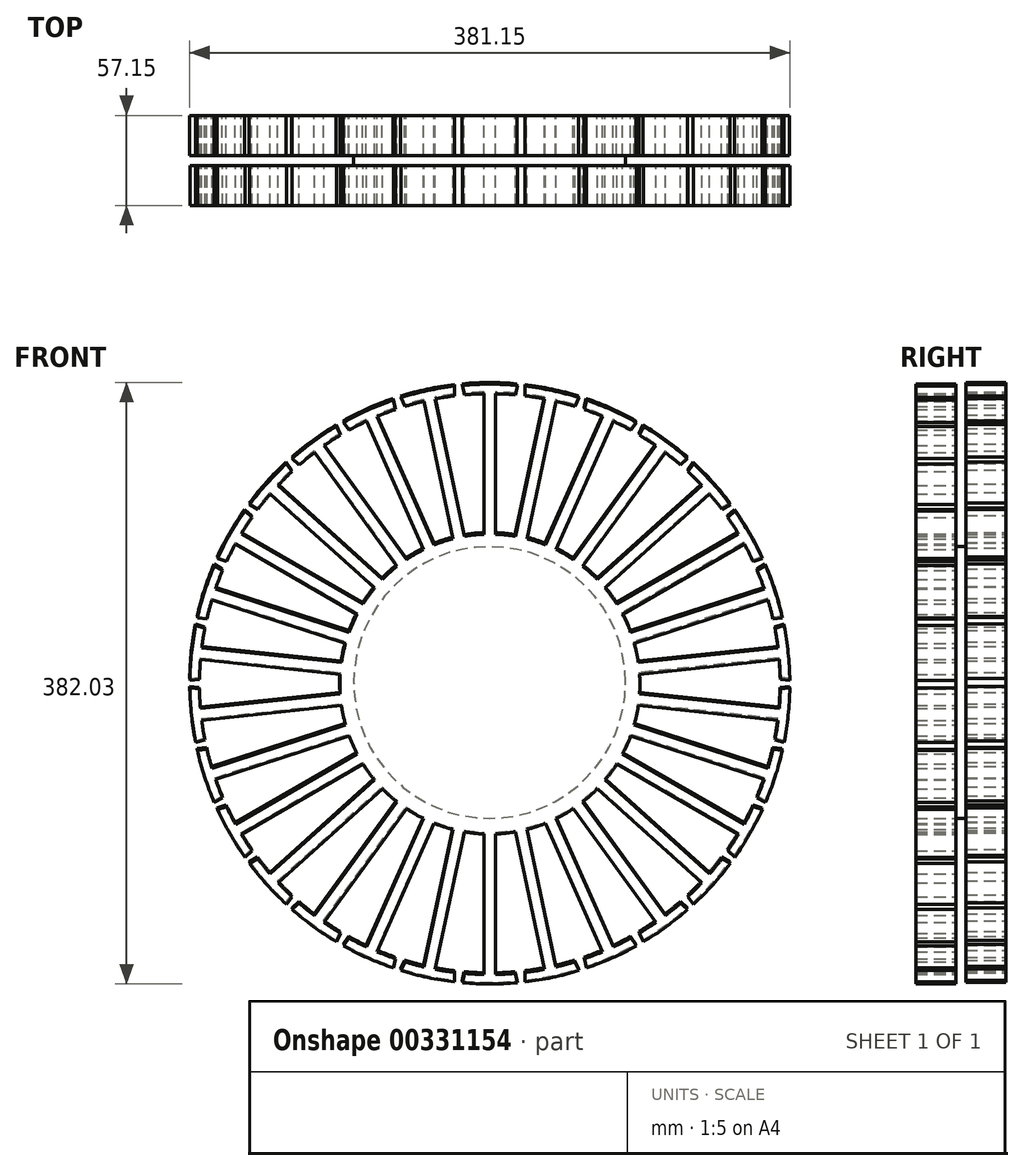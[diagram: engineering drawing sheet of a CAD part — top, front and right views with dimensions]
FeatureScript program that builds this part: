
annotation { "Feature Type Name" : "Feature", "Feature Type Description" : "" }
export const myFeature = defineFeature(function(context is Context, id is Id, definition is map)
    precondition{}
    {
        {
            var Q0;
            Q0=qCreatedBy(makeId("Front.planeOp"),FACE);
            var sketch = newSketch(context, id + "F0", { "sketchPlane" : qUnion([Q0])});
            skArc(sketch, "E0", {"start": v(17.45, 189.7) * mm, "mid": v(0, 190.5) * mm, "end": v(-17.45, 189.7) * mm});
            skArc(sketch, "E1", {"start": v(-3.7, 95.18) * mm, "mid": v(0, -95.25) * mm, "end": v(3.7, 95.18) * mm});
            skArc(sketch, "E2", {"start": v(-3.7, 184.44) * mm, "mid": v(-9.96, 184.2) * mm, "end": v(-16.2, 183.77) * mm});
            skLineSegment(sketch, "E3.left", {"start": v(3.7, 184.44) * mm, "end": v(3.7, 95.18) * mm});
            skLineSegment(sketch, "E3.right", {"start": v(-3.7, 184.44) * mm, "end": v(-3.7, 95.18) * mm});
            skPoint(sketch, "E3.middle", {"position": v(0, 139.8) * mm});
            skLineSegment(sketch, "E4", {"start": v(-17.45, 189.7) * mm, "end": v(-16.2, 183.77) * mm});
            skLineSegment(sketch, "E5.MirrorCS", {"start": v(17.45, 189.7) * mm, "end": v(16.2, 183.77) * mm});
            skArc(sketch, "E6.trimOffspring", {"start": v(16.2, 183.77) * mm, "mid": v(9.96, 184.2) * mm, "end": v(3.7, 184.44) * mm});
            skArc(sketch, "E7.1.0", {"start": v(-22.38, 189.18) * mm, "mid": v(-39.6, 186.34) * mm, "end": v(-56.5, 181.93) * mm});
            skLineSegment(sketch, "E7.1.1", {"start": v(-56.5, 181.93) * mm, "end": v(-54.05, 176.38) * mm});
            skArc(sketch, "E7.1.2", {"start": v(-41.97, 179.64) * mm, "mid": v(-48.04, 178.11) * mm, "end": v(-54.05, 176.38) * mm});
            skArc(sketch, "E7.1.3", {"start": v(-22.36, 183.12) * mm, "mid": v(-28.56, 182.25) * mm, "end": v(-34.73, 181.18) * mm});
            skLineSegment(sketch, "E7.1.4", {"start": v(-22.38, 189.18) * mm, "end": v(-22.36, 183.12) * mm});
            skLineSegment(sketch, "E7.1.5", {"start": v(-34.73, 181.18) * mm, "end": v(-16.17, 93.87) * mm});
            skLineSegment(sketch, "E7.1.6", {"start": v(-41.97, 179.64) * mm, "end": v(-23.41, 92.33) * mm});
            skArc(sketch, "E8.3.2.0", {"start": v(-61.22, 180.4) * mm, "mid": v(-77.48, 174.03) * mm, "end": v(-93.1, 166.2) * mm});
            skLineSegment(sketch, "E8.4.2.0", {"start": v(-93.1, 166.2) * mm, "end": v(-89.54, 161.29) * mm});
            skArc(sketch, "E8.7.2.0", {"start": v(-78.4, 166.99) * mm, "mid": v(-84.02, 164.23) * mm, "end": v(-89.54, 161.29) * mm});
            skArc(sketch, "E8.11.2.0", {"start": v(-59.95, 174.47) * mm, "mid": v(-65.83, 172.33) * mm, "end": v(-71.64, 170) * mm});
            skLineSegment(sketch, "E8.15.2.0", {"start": v(-61.22, 180.4) * mm, "end": v(-59.95, 174.47) * mm});
            skLineSegment(sketch, "E8.18.2.0", {"start": v(-71.64, 170) * mm, "end": v(-35.33, 88.46) * mm});
            skLineSegment(sketch, "E8.21.2.0", {"start": v(-78.4, 166.99) * mm, "end": v(-42.1, 85.44) * mm});
            skArc(sketch, "E8.3.3.0", {"start": v(-97.39, 163.72) * mm, "mid": v(-111.97, 154.12) * mm, "end": v(-125.62, 143.22) * mm});
            skLineSegment(sketch, "E8.4.3.0", {"start": v(-125.62, 143.22) * mm, "end": v(-121.12, 139.15) * mm});
            skArc(sketch, "E8.7.3.0", {"start": v(-111.4, 147.04) * mm, "mid": v(-116.33, 143.18) * mm, "end": v(-121.12, 139.15) * mm});
            skArc(sketch, "E8.11.3.0", {"start": v(-94.9, 158.2) * mm, "mid": v(-100.22, 154.88) * mm, "end": v(-105.42, 151.4) * mm});
            skLineSegment(sketch, "E8.15.3.0", {"start": v(-97.39, 163.72) * mm, "end": v(-94.9, 158.2) * mm});
            skLineSegment(sketch, "E8.18.3.0", {"start": v(-105.42, 151.4) * mm, "end": v(-52.95, 79.18) * mm});
            skLineSegment(sketch, "E8.21.3.0", {"start": v(-111.4, 147.04) * mm, "end": v(-58.94, 74.82) * mm});
            skArc(sketch, "E8.3.4.0", {"start": v(-129.3, 139.9) * mm, "mid": v(-141.57, 127.47) * mm, "end": v(-152.65, 113.97) * mm});
            skLineSegment(sketch, "E8.4.4.0", {"start": v(-152.65, 113.97) * mm, "end": v(-147.4, 110.92) * mm});
            skArc(sketch, "E8.7.4.0", {"start": v(-139.54, 120.66) * mm, "mid": v(-143.56, 115.86) * mm, "end": v(-147.4, 110.92) * mm});
            skArc(sketch, "E8.11.4.0", {"start": v(-125.72, 135) * mm, "mid": v(-130.23, 130.66) * mm, "end": v(-134.59, 126.17) * mm});
            skLineSegment(sketch, "E8.15.4.0", {"start": v(-129.3, 139.9) * mm, "end": v(-125.72, 135) * mm});
            skLineSegment(sketch, "E8.18.4.0", {"start": v(-134.59, 126.17) * mm, "end": v(-68.25, 66.44) * mm});
            skLineSegment(sketch, "E8.21.4.0", {"start": v(-139.54, 120.66) * mm, "end": v(-73.2, 60.93) * mm});
            skArc(sketch, "E8.3.5.0", {"start": v(-155.56, 109.96) * mm, "mid": v(-164.98, 95.25) * mm, "end": v(-173, 79.74) * mm});
            skLineSegment(sketch, "E8.4.5.0", {"start": v(-173, 79.74) * mm, "end": v(-167.24, 77.85) * mm});
            skArc(sketch, "E8.7.5.0", {"start": v(-161.58, 89.01) * mm, "mid": v(-164.5, 83.48) * mm, "end": v(-167.24, 77.85) * mm});
            skArc(sketch, "E8.11.5.0", {"start": v(-151.05, 105.91) * mm, "mid": v(-154.55, 100.73) * mm, "end": v(-157.88, 95.43) * mm});
            skLineSegment(sketch, "E8.15.5.0", {"start": v(-155.56, 109.96) * mm, "end": v(-151.05, 105.91) * mm});
            skLineSegment(sketch, "E8.18.5.0", {"start": v(-157.88, 95.43) * mm, "end": v(-80.57, 50.8) * mm});
            skLineSegment(sketch, "E8.21.5.0", {"start": v(-161.58, 89.01) * mm, "end": v(-84.28, 44.38) * mm});
            skArc(sketch, "E8.3.6.0", {"start": v(-175.02, 75.21) * mm, "mid": v(-181.18, 58.87) * mm, "end": v(-185.8, 42.03) * mm});
            skLineSegment(sketch, "E8.4.6.0", {"start": v(-185.8, 42.03) * mm, "end": v(-179.78, 41.38) * mm});
            skArc(sketch, "E8.7.6.0", {"start": v(-176.56, 53.47) * mm, "mid": v(-178.27, 47.45) * mm, "end": v(-179.78, 41.38) * mm});
            skArc(sketch, "E8.11.6.0", {"start": v(-169.77, 72.2) * mm, "mid": v(-172.12, 66.4) * mm, "end": v(-174.27, 60.52) * mm});
            skLineSegment(sketch, "E8.15.6.0", {"start": v(-175.02, 75.21) * mm, "end": v(-169.77, 72.2) * mm});
            skLineSegment(sketch, "E8.18.6.0", {"start": v(-174.27, 60.52) * mm, "end": v(-89.38, 32.93) * mm});
            skLineSegment(sketch, "E8.21.6.0", {"start": v(-176.56, 53.47) * mm, "end": v(-91.66, 25.89) * mm});
            skArc(sketch, "E8.3.7.0", {"start": v(-186.84, 37.18) * mm, "mid": v(-189.46, 19.91) * mm, "end": v(-190.48, 2.48) * mm});
            skLineSegment(sketch, "E8.4.7.0", {"start": v(-190.48, 2.48) * mm, "end": v(-184.45, 3.1) * mm});
            skArc(sketch, "E8.7.7.0", {"start": v(-183.82, 15.6) * mm, "mid": v(-184.24, 9.35) * mm, "end": v(-184.45, 3.1) * mm});
            skArc(sketch, "E8.11.7.0", {"start": v(-181.07, 35.32) * mm, "mid": v(-182.16, 29.16) * mm, "end": v(-183.04, 22.96) * mm});
            skLineSegment(sketch, "E8.15.7.0", {"start": v(-186.84, 37.18) * mm, "end": v(-181.07, 35.32) * mm});
            skLineSegment(sketch, "E8.18.7.0", {"start": v(-183.04, 22.96) * mm, "end": v(-94.27, 13.63) * mm});
            skLineSegment(sketch, "E8.21.7.0", {"start": v(-183.82, 15.6) * mm, "end": v(-95.04, 6.27) * mm});
            skArc(sketch, "E8.3.8.0", {"start": v(-190.48, -2.48) * mm, "mid": v(-189.46, -19.91) * mm, "end": v(-186.84, -37.18) * mm});
            skLineSegment(sketch, "E8.4.8.0", {"start": v(-186.84, -37.18) * mm, "end": v(-181.07, -35.32) * mm});
            skArc(sketch, "E8.7.8.0", {"start": v(-183.04, -22.96) * mm, "mid": v(-182.16, -29.16) * mm, "end": v(-181.07, -35.32) * mm});
            skArc(sketch, "E8.11.8.0", {"start": v(-184.45, -3.1) * mm, "mid": v(-184.24, -9.35) * mm, "end": v(-183.82, -15.6) * mm});
            skLineSegment(sketch, "E8.15.8.0", {"start": v(-190.48, -2.48) * mm, "end": v(-184.45, -3.1) * mm});
            skLineSegment(sketch, "E8.18.8.0", {"start": v(-183.82, -15.6) * mm, "end": v(-95.04, -6.27) * mm});
            skLineSegment(sketch, "E8.21.8.0", {"start": v(-183.04, -22.96) * mm, "end": v(-94.27, -13.63) * mm});
            skArc(sketch, "E8.3.9.0", {"start": v(-185.8, -42.03) * mm, "mid": v(-181.18, -58.87) * mm, "end": v(-175.02, -75.21) * mm});
            skLineSegment(sketch, "E8.4.9.0", {"start": v(-175.02, -75.21) * mm, "end": v(-169.77, -72.2) * mm});
            skArc(sketch, "E8.7.9.0", {"start": v(-174.27, -60.52) * mm, "mid": v(-172.12, -66.4) * mm, "end": v(-169.77, -72.2) * mm});
            skArc(sketch, "E8.11.9.0", {"start": v(-179.78, -41.38) * mm, "mid": v(-178.27, -47.45) * mm, "end": v(-176.56, -53.47) * mm});
            skLineSegment(sketch, "E8.15.9.0", {"start": v(-185.8, -42.03) * mm, "end": v(-179.78, -41.38) * mm});
            skLineSegment(sketch, "E8.18.9.0", {"start": v(-176.56, -53.47) * mm, "end": v(-91.66, -25.89) * mm});
            skLineSegment(sketch, "E8.21.9.0", {"start": v(-174.27, -60.52) * mm, "end": v(-89.38, -32.93) * mm});
            skArc(sketch, "E8.3.10.0", {"start": v(-173, -79.74) * mm, "mid": v(-164.98, -95.25) * mm, "end": v(-155.56, -109.96) * mm});
            skLineSegment(sketch, "E8.4.10.0", {"start": v(-155.56, -109.96) * mm, "end": v(-151.05, -105.91) * mm});
            skArc(sketch, "E8.7.10.0", {"start": v(-157.88, -95.43) * mm, "mid": v(-154.55, -100.73) * mm, "end": v(-151.05, -105.91) * mm});
            skArc(sketch, "E8.11.10.0", {"start": v(-167.24, -77.85) * mm, "mid": v(-164.5, -83.48) * mm, "end": v(-161.58, -89.01) * mm});
            skLineSegment(sketch, "E8.15.10.0", {"start": v(-173, -79.74) * mm, "end": v(-167.24, -77.85) * mm});
            skLineSegment(sketch, "E8.18.10.0", {"start": v(-161.58, -89.01) * mm, "end": v(-84.28, -44.38) * mm});
            skLineSegment(sketch, "E8.21.10.0", {"start": v(-157.88, -95.43) * mm, "end": v(-80.57, -50.8) * mm});
            skArc(sketch, "E8.3.11.0", {"start": v(-152.65, -113.97) * mm, "mid": v(-141.57, -127.47) * mm, "end": v(-129.3, -139.9) * mm});
            skLineSegment(sketch, "E8.4.11.0", {"start": v(-129.3, -139.9) * mm, "end": v(-125.72, -135) * mm});
            skArc(sketch, "E8.7.11.0", {"start": v(-134.59, -126.17) * mm, "mid": v(-130.23, -130.66) * mm, "end": v(-125.72, -135) * mm});
            skArc(sketch, "E8.11.11.0", {"start": v(-147.4, -110.92) * mm, "mid": v(-143.56, -115.86) * mm, "end": v(-139.54, -120.66) * mm});
            skLineSegment(sketch, "E8.15.11.0", {"start": v(-152.65, -113.97) * mm, "end": v(-147.4, -110.92) * mm});
            skLineSegment(sketch, "E8.18.11.0", {"start": v(-139.54, -120.66) * mm, "end": v(-73.2, -60.93) * mm});
            skLineSegment(sketch, "E8.21.11.0", {"start": v(-134.59, -126.17) * mm, "end": v(-68.25, -66.44) * mm});
            skArc(sketch, "E8.3.12.0", {"start": v(-125.62, -143.22) * mm, "mid": v(-111.97, -154.12) * mm, "end": v(-97.39, -163.72) * mm});
            skLineSegment(sketch, "E8.4.12.0", {"start": v(-97.39, -163.72) * mm, "end": v(-94.9, -158.2) * mm});
            skArc(sketch, "E8.7.12.0", {"start": v(-105.42, -151.4) * mm, "mid": v(-100.22, -154.88) * mm, "end": v(-94.9, -158.2) * mm});
            skArc(sketch, "E8.11.12.0", {"start": v(-121.12, -139.15) * mm, "mid": v(-116.33, -143.18) * mm, "end": v(-111.4, -147.04) * mm});
            skLineSegment(sketch, "E8.15.12.0", {"start": v(-125.62, -143.22) * mm, "end": v(-121.12, -139.15) * mm});
            skLineSegment(sketch, "E8.18.12.0", {"start": v(-111.4, -147.04) * mm, "end": v(-58.94, -74.82) * mm});
            skLineSegment(sketch, "E8.21.12.0", {"start": v(-105.42, -151.4) * mm, "end": v(-52.95, -79.18) * mm});
            skArc(sketch, "E8.3.13.0", {"start": v(-93.1, -166.2) * mm, "mid": v(-77.48, -174.03) * mm, "end": v(-61.22, -180.4) * mm});
            skLineSegment(sketch, "E8.4.13.0", {"start": v(-61.22, -180.4) * mm, "end": v(-59.95, -174.47) * mm});
            skArc(sketch, "E8.7.13.0", {"start": v(-71.64, -170) * mm, "mid": v(-65.83, -172.33) * mm, "end": v(-59.95, -174.47) * mm});
            skArc(sketch, "E8.11.13.0", {"start": v(-89.54, -161.29) * mm, "mid": v(-84.02, -164.23) * mm, "end": v(-78.4, -166.99) * mm});
            skLineSegment(sketch, "E8.15.13.0", {"start": v(-93.1, -166.2) * mm, "end": v(-89.54, -161.29) * mm});
            skLineSegment(sketch, "E8.18.13.0", {"start": v(-78.4, -166.99) * mm, "end": v(-42.1, -85.44) * mm});
            skLineSegment(sketch, "E8.21.13.0", {"start": v(-71.64, -170) * mm, "end": v(-35.33, -88.46) * mm});
            skArc(sketch, "E8.3.14.0", {"start": v(-56.5, -181.93) * mm, "mid": v(-39.6, -186.34) * mm, "end": v(-22.38, -189.18) * mm});
            skLineSegment(sketch, "E8.4.14.0", {"start": v(-22.38, -189.18) * mm, "end": v(-22.36, -183.12) * mm});
            skArc(sketch, "E8.7.14.0", {"start": v(-34.73, -181.18) * mm, "mid": v(-28.56, -182.25) * mm, "end": v(-22.36, -183.12) * mm});
            skArc(sketch, "E8.11.14.0", {"start": v(-54.05, -176.38) * mm, "mid": v(-48.04, -178.11) * mm, "end": v(-41.97, -179.64) * mm});
            skLineSegment(sketch, "E8.15.14.0", {"start": v(-56.5, -181.93) * mm, "end": v(-54.05, -176.38) * mm});
            skLineSegment(sketch, "E8.18.14.0", {"start": v(-41.97, -179.64) * mm, "end": v(-23.41, -92.33) * mm});
            skLineSegment(sketch, "E8.21.14.0", {"start": v(-34.73, -181.18) * mm, "end": v(-16.17, -93.87) * mm});
            skArc(sketch, "E8.3.15.0", {"start": v(-17.45, -189.7) * mm, "mid": v(0, -190.5) * mm, "end": v(17.45, -189.7) * mm});
            skLineSegment(sketch, "E8.4.15.0", {"start": v(17.45, -189.7) * mm, "end": v(16.2, -183.77) * mm});
            skArc(sketch, "E8.7.15.0", {"start": v(3.7, -184.44) * mm, "mid": v(9.96, -184.2) * mm, "end": v(16.2, -183.77) * mm});
            skArc(sketch, "E8.11.15.0", {"start": v(-16.2, -183.77) * mm, "mid": v(-9.96, -184.2) * mm, "end": v(-3.7, -184.44) * mm});
            skLineSegment(sketch, "E8.15.15.0", {"start": v(-17.45, -189.7) * mm, "end": v(-16.2, -183.77) * mm});
            skLineSegment(sketch, "E8.18.15.0", {"start": v(-3.7, -184.44) * mm, "end": v(-3.7, -95.18) * mm});
            skLineSegment(sketch, "E8.21.15.0", {"start": v(3.7, -184.44) * mm, "end": v(3.7, -95.18) * mm});
            skArc(sketch, "E8.3.16.0", {"start": v(22.38, -189.18) * mm, "mid": v(39.6, -186.34) * mm, "end": v(56.5, -181.93) * mm});
            skLineSegment(sketch, "E8.4.16.0", {"start": v(56.5, -181.93) * mm, "end": v(54.05, -176.38) * mm});
            skArc(sketch, "E8.7.16.0", {"start": v(41.97, -179.64) * mm, "mid": v(48.04, -178.11) * mm, "end": v(54.05, -176.38) * mm});
            skArc(sketch, "E8.11.16.0", {"start": v(22.36, -183.12) * mm, "mid": v(28.56, -182.25) * mm, "end": v(34.73, -181.18) * mm});
            skLineSegment(sketch, "E8.15.16.0", {"start": v(22.38, -189.18) * mm, "end": v(22.36, -183.12) * mm});
            skLineSegment(sketch, "E8.18.16.0", {"start": v(34.73, -181.18) * mm, "end": v(16.17, -93.87) * mm});
            skLineSegment(sketch, "E8.21.16.0", {"start": v(41.97, -179.64) * mm, "end": v(23.41, -92.33) * mm});
            skArc(sketch, "E8.3.17.0", {"start": v(61.22, -180.4) * mm, "mid": v(77.48, -174.03) * mm, "end": v(93.1, -166.2) * mm});
            skLineSegment(sketch, "E8.4.17.0", {"start": v(93.1, -166.2) * mm, "end": v(89.54, -161.29) * mm});
            skArc(sketch, "E8.7.17.0", {"start": v(78.4, -166.99) * mm, "mid": v(84.02, -164.23) * mm, "end": v(89.54, -161.29) * mm});
            skArc(sketch, "E8.11.17.0", {"start": v(59.95, -174.47) * mm, "mid": v(65.83, -172.33) * mm, "end": v(71.64, -170) * mm});
            skLineSegment(sketch, "E8.15.17.0", {"start": v(61.22, -180.4) * mm, "end": v(59.95, -174.47) * mm});
            skLineSegment(sketch, "E8.18.17.0", {"start": v(71.64, -170) * mm, "end": v(35.33, -88.46) * mm});
            skLineSegment(sketch, "E8.21.17.0", {"start": v(78.4, -166.99) * mm, "end": v(42.1, -85.44) * mm});
            skArc(sketch, "E8.3.18.0", {"start": v(97.39, -163.72) * mm, "mid": v(111.97, -154.12) * mm, "end": v(125.62, -143.22) * mm});
            skLineSegment(sketch, "E8.4.18.0", {"start": v(125.62, -143.22) * mm, "end": v(121.12, -139.15) * mm});
            skArc(sketch, "E8.7.18.0", {"start": v(111.4, -147.04) * mm, "mid": v(116.33, -143.18) * mm, "end": v(121.12, -139.15) * mm});
            skArc(sketch, "E8.11.18.0", {"start": v(94.9, -158.2) * mm, "mid": v(100.22, -154.88) * mm, "end": v(105.42, -151.4) * mm});
            skLineSegment(sketch, "E8.15.18.0", {"start": v(97.39, -163.72) * mm, "end": v(94.9, -158.2) * mm});
            skLineSegment(sketch, "E8.18.18.0", {"start": v(105.42, -151.4) * mm, "end": v(52.95, -79.18) * mm});
            skLineSegment(sketch, "E8.21.18.0", {"start": v(111.4, -147.04) * mm, "end": v(58.94, -74.82) * mm});
            skArc(sketch, "E8.3.19.0", {"start": v(129.3, -139.9) * mm, "mid": v(141.57, -127.47) * mm, "end": v(152.65, -113.97) * mm});
            skLineSegment(sketch, "E8.4.19.0", {"start": v(152.65, -113.97) * mm, "end": v(147.4, -110.92) * mm});
            skArc(sketch, "E8.7.19.0", {"start": v(139.54, -120.66) * mm, "mid": v(143.56, -115.86) * mm, "end": v(147.4, -110.92) * mm});
            skArc(sketch, "E8.11.19.0", {"start": v(125.72, -135) * mm, "mid": v(130.23, -130.66) * mm, "end": v(134.59, -126.17) * mm});
            skLineSegment(sketch, "E8.15.19.0", {"start": v(129.3, -139.9) * mm, "end": v(125.72, -135) * mm});
            skLineSegment(sketch, "E8.18.19.0", {"start": v(134.59, -126.17) * mm, "end": v(68.25, -66.44) * mm});
            skLineSegment(sketch, "E8.21.19.0", {"start": v(139.54, -120.66) * mm, "end": v(73.2, -60.93) * mm});
            skArc(sketch, "E8.3.20.0", {"start": v(155.56, -109.96) * mm, "mid": v(164.98, -95.25) * mm, "end": v(173, -79.74) * mm});
            skLineSegment(sketch, "E8.4.20.0", {"start": v(173, -79.74) * mm, "end": v(167.24, -77.85) * mm});
            skArc(sketch, "E8.7.20.0", {"start": v(161.58, -89.01) * mm, "mid": v(164.5, -83.48) * mm, "end": v(167.24, -77.85) * mm});
            skArc(sketch, "E8.11.20.0", {"start": v(151.05, -105.91) * mm, "mid": v(154.55, -100.73) * mm, "end": v(157.88, -95.43) * mm});
            skLineSegment(sketch, "E8.15.20.0", {"start": v(155.56, -109.96) * mm, "end": v(151.05, -105.91) * mm});
            skLineSegment(sketch, "E8.18.20.0", {"start": v(157.88, -95.43) * mm, "end": v(80.57, -50.8) * mm});
            skLineSegment(sketch, "E8.21.20.0", {"start": v(161.58, -89.01) * mm, "end": v(84.28, -44.38) * mm});
            skArc(sketch, "E8.3.21.0", {"start": v(175.02, -75.21) * mm, "mid": v(181.18, -58.87) * mm, "end": v(185.8, -42.03) * mm});
            skLineSegment(sketch, "E8.4.21.0", {"start": v(185.8, -42.03) * mm, "end": v(179.78, -41.38) * mm});
            skArc(sketch, "E8.7.21.0", {"start": v(176.56, -53.47) * mm, "mid": v(178.27, -47.45) * mm, "end": v(179.78, -41.38) * mm});
            skArc(sketch, "E8.11.21.0", {"start": v(169.77, -72.2) * mm, "mid": v(172.12, -66.4) * mm, "end": v(174.27, -60.52) * mm});
            skLineSegment(sketch, "E8.15.21.0", {"start": v(175.02, -75.21) * mm, "end": v(169.77, -72.2) * mm});
            skLineSegment(sketch, "E8.18.21.0", {"start": v(174.27, -60.52) * mm, "end": v(89.38, -32.93) * mm});
            skLineSegment(sketch, "E8.21.21.0", {"start": v(176.56, -53.47) * mm, "end": v(91.66, -25.89) * mm});
            skArc(sketch, "E8.3.22.0", {"start": v(186.84, -37.18) * mm, "mid": v(189.46, -19.91) * mm, "end": v(190.48, -2.48) * mm});
            skLineSegment(sketch, "E8.4.22.0", {"start": v(190.48, -2.48) * mm, "end": v(184.45, -3.1) * mm});
            skArc(sketch, "E8.7.22.0", {"start": v(183.82, -15.6) * mm, "mid": v(184.24, -9.35) * mm, "end": v(184.45, -3.1) * mm});
            skArc(sketch, "E8.11.22.0", {"start": v(181.07, -35.32) * mm, "mid": v(182.16, -29.16) * mm, "end": v(183.04, -22.96) * mm});
            skLineSegment(sketch, "E8.15.22.0", {"start": v(186.84, -37.18) * mm, "end": v(181.07, -35.32) * mm});
            skLineSegment(sketch, "E8.18.22.0", {"start": v(183.04, -22.96) * mm, "end": v(94.27, -13.63) * mm});
            skLineSegment(sketch, "E8.21.22.0", {"start": v(183.82, -15.6) * mm, "end": v(95.04, -6.27) * mm});
            skArc(sketch, "E8.3.23.0", {"start": v(190.48, 2.48) * mm, "mid": v(189.46, 19.91) * mm, "end": v(186.84, 37.18) * mm});
            skLineSegment(sketch, "E8.4.23.0", {"start": v(186.84, 37.18) * mm, "end": v(181.07, 35.32) * mm});
            skArc(sketch, "E8.7.23.0", {"start": v(183.04, 22.96) * mm, "mid": v(182.16, 29.16) * mm, "end": v(181.07, 35.32) * mm});
            skArc(sketch, "E8.11.23.0", {"start": v(184.45, 3.1) * mm, "mid": v(184.24, 9.35) * mm, "end": v(183.82, 15.6) * mm});
            skLineSegment(sketch, "E8.15.23.0", {"start": v(190.48, 2.48) * mm, "end": v(184.45, 3.1) * mm});
            skLineSegment(sketch, "E8.18.23.0", {"start": v(183.82, 15.6) * mm, "end": v(95.04, 6.27) * mm});
            skLineSegment(sketch, "E8.21.23.0", {"start": v(183.04, 22.96) * mm, "end": v(94.27, 13.63) * mm});
            skArc(sketch, "E8.3.24.0", {"start": v(185.8, 42.03) * mm, "mid": v(181.18, 58.87) * mm, "end": v(175.02, 75.21) * mm});
            skLineSegment(sketch, "E8.4.24.0", {"start": v(175.02, 75.21) * mm, "end": v(169.77, 72.2) * mm});
            skArc(sketch, "E8.7.24.0", {"start": v(174.27, 60.52) * mm, "mid": v(172.12, 66.4) * mm, "end": v(169.77, 72.2) * mm});
            skArc(sketch, "E8.11.24.0", {"start": v(179.78, 41.38) * mm, "mid": v(178.27, 47.45) * mm, "end": v(176.56, 53.47) * mm});
            skLineSegment(sketch, "E8.15.24.0", {"start": v(185.8, 42.03) * mm, "end": v(179.78, 41.38) * mm});
            skLineSegment(sketch, "E8.18.24.0", {"start": v(176.56, 53.47) * mm, "end": v(91.66, 25.89) * mm});
            skLineSegment(sketch, "E8.21.24.0", {"start": v(174.27, 60.52) * mm, "end": v(89.38, 32.93) * mm});
            skArc(sketch, "E8.3.25.0", {"start": v(173, 79.74) * mm, "mid": v(164.98, 95.25) * mm, "end": v(155.56, 109.96) * mm});
            skLineSegment(sketch, "E8.4.25.0", {"start": v(155.56, 109.96) * mm, "end": v(151.05, 105.91) * mm});
            skArc(sketch, "E8.7.25.0", {"start": v(157.88, 95.43) * mm, "mid": v(154.55, 100.73) * mm, "end": v(151.05, 105.91) * mm});
            skArc(sketch, "E8.11.25.0", {"start": v(167.24, 77.85) * mm, "mid": v(164.5, 83.48) * mm, "end": v(161.58, 89.01) * mm});
            skLineSegment(sketch, "E8.15.25.0", {"start": v(173, 79.74) * mm, "end": v(167.24, 77.85) * mm});
            skLineSegment(sketch, "E8.18.25.0", {"start": v(161.58, 89.01) * mm, "end": v(84.28, 44.38) * mm});
            skLineSegment(sketch, "E8.21.25.0", {"start": v(157.88, 95.43) * mm, "end": v(80.57, 50.8) * mm});
            skArc(sketch, "E8.3.26.0", {"start": v(152.65, 113.97) * mm, "mid": v(141.57, 127.47) * mm, "end": v(129.3, 139.9) * mm});
            skLineSegment(sketch, "E8.4.26.0", {"start": v(129.3, 139.9) * mm, "end": v(125.72, 135) * mm});
            skArc(sketch, "E8.7.26.0", {"start": v(134.59, 126.17) * mm, "mid": v(130.23, 130.66) * mm, "end": v(125.72, 135) * mm});
            skArc(sketch, "E8.11.26.0", {"start": v(147.4, 110.92) * mm, "mid": v(143.56, 115.86) * mm, "end": v(139.54, 120.66) * mm});
            skLineSegment(sketch, "E8.15.26.0", {"start": v(152.65, 113.97) * mm, "end": v(147.4, 110.92) * mm});
            skLineSegment(sketch, "E8.18.26.0", {"start": v(139.54, 120.66) * mm, "end": v(73.2, 60.93) * mm});
            skLineSegment(sketch, "E8.21.26.0", {"start": v(134.59, 126.17) * mm, "end": v(68.25, 66.44) * mm});
            skArc(sketch, "E8.3.27.0", {"start": v(125.62, 143.22) * mm, "mid": v(111.97, 154.12) * mm, "end": v(97.39, 163.72) * mm});
            skLineSegment(sketch, "E8.4.27.0", {"start": v(97.39, 163.72) * mm, "end": v(94.9, 158.2) * mm});
            skArc(sketch, "E8.7.27.0", {"start": v(105.42, 151.4) * mm, "mid": v(100.22, 154.88) * mm, "end": v(94.9, 158.2) * mm});
            skArc(sketch, "E8.11.27.0", {"start": v(121.12, 139.15) * mm, "mid": v(116.33, 143.18) * mm, "end": v(111.4, 147.04) * mm});
            skLineSegment(sketch, "E8.15.27.0", {"start": v(125.62, 143.22) * mm, "end": v(121.12, 139.15) * mm});
            skLineSegment(sketch, "E8.18.27.0", {"start": v(111.4, 147.04) * mm, "end": v(58.94, 74.82) * mm});
            skLineSegment(sketch, "E8.21.27.0", {"start": v(105.42, 151.4) * mm, "end": v(52.95, 79.18) * mm});
            skArc(sketch, "E8.3.28.0", {"start": v(93.1, 166.2) * mm, "mid": v(77.48, 174.03) * mm, "end": v(61.22, 180.4) * mm});
            skLineSegment(sketch, "E8.4.28.0", {"start": v(61.22, 180.4) * mm, "end": v(59.95, 174.47) * mm});
            skArc(sketch, "E8.7.28.0", {"start": v(71.64, 170) * mm, "mid": v(65.83, 172.33) * mm, "end": v(59.95, 174.47) * mm});
            skArc(sketch, "E8.11.28.0", {"start": v(89.54, 161.29) * mm, "mid": v(84.02, 164.23) * mm, "end": v(78.4, 166.99) * mm});
            skLineSegment(sketch, "E8.15.28.0", {"start": v(93.1, 166.2) * mm, "end": v(89.54, 161.29) * mm});
            skLineSegment(sketch, "E8.18.28.0", {"start": v(78.4, 166.99) * mm, "end": v(42.1, 85.44) * mm});
            skLineSegment(sketch, "E8.21.28.0", {"start": v(71.64, 170) * mm, "end": v(35.33, 88.46) * mm});
            skArc(sketch, "E8.3.29.0", {"start": v(56.5, 181.93) * mm, "mid": v(39.6, 186.34) * mm, "end": v(22.38, 189.18) * mm});
            skLineSegment(sketch, "E8.4.29.0", {"start": v(22.38, 189.18) * mm, "end": v(22.36, 183.12) * mm});
            skArc(sketch, "E8.7.29.0", {"start": v(34.73, 181.18) * mm, "mid": v(28.56, 182.25) * mm, "end": v(22.36, 183.12) * mm});
            skArc(sketch, "E8.11.29.0", {"start": v(54.05, 176.38) * mm, "mid": v(48.04, 178.11) * mm, "end": v(41.97, 179.64) * mm});
            skLineSegment(sketch, "E8.15.29.0", {"start": v(56.5, 181.93) * mm, "end": v(54.05, 176.38) * mm});
            skLineSegment(sketch, "E8.18.29.0", {"start": v(41.97, 179.64) * mm, "end": v(23.41, 92.33) * mm});
            skLineSegment(sketch, "E8.21.29.0", {"start": v(34.73, 181.18) * mm, "end": v(16.17, 93.87) * mm});
            skSolve(sketch);
        }
        {
            var Q0;
            Q0=makeQuery(id+"F0.imprint","IMPRINT",FACE,{"disambiguationData":[TD([[makeQuery(id+"F0.imprint","IMPRINT",EDGE,{"derivedFrom":sQuery(id+"F0.wireOp",EDGE,"E0")}),1.0]])]});
            var Q1;
            Q1=makeQuery(id+"F0.imprint","IMPRINT",FACE,{"disambiguationData":[TD([[makeQuery(id+"F0.imprint","IMPRINT",EDGE,{"derivedFrom":sQuery(id+"F0.wireOp",EDGE,"E7.1.0")}),1.0]])]});
            var Q2;
            Q2=makeQuery(id+"F0.imprint","IMPRINT",FACE,{"disambiguationData":[TD([[makeQuery(id+"F0.imprint","IMPRINT",EDGE,{"derivedFrom":sQuery(id+"F0.wireOp",EDGE,"76a48f0a-06ff-47b8-89dc-eab9dbdf2e76.3.29.0")}),1.0]])]});
            var Q3;
            Q3=makeQuery(id+"F0.imprint","IMPRINT",FACE,{"disambiguationData":[TD([[makeQuery(id+"F0.imprint","IMPRINT",EDGE,{"derivedFrom":sQuery(id+"F0.wireOp",EDGE,"76a48f0a-06ff-47b8-89dc-eab9dbdf2e76.3.28.0")}),1.0]])]});
            var Q4;
            Q4=makeQuery(id+"F0.imprint","IMPRINT",FACE,{"disambiguationData":[TD([[makeQuery(id+"F0.imprint","IMPRINT",EDGE,{"derivedFrom":sQuery(id+"F0.wireOp",EDGE,"76a48f0a-06ff-47b8-89dc-eab9dbdf2e76.3.27.0")}),1.0]])]});
            var Q5;
            Q5=makeQuery(id+"F0.imprint","IMPRINT",FACE,{"disambiguationData":[TD([[makeQuery(id+"F0.imprint","IMPRINT",EDGE,{"derivedFrom":sQuery(id+"F0.wireOp",EDGE,"74bc0bd4-5262-492f-8b10-774244a7f6fe.3.26.0")}),1.0]])]});
            var Q6;
            Q6=makeQuery(id+"F0.imprint","IMPRINT",FACE,{"disambiguationData":[TD([[makeQuery(id+"F0.imprint","IMPRINT",EDGE,{"derivedFrom":sQuery(id+"F0.wireOp",EDGE,"74bc0bd4-5262-492f-8b10-774244a7f6fe.3.25.0")}),1.0]])]});
            var Q7;
            Q7=makeQuery(id+"F0.imprint","IMPRINT",FACE,{"disambiguationData":[TD([[makeQuery(id+"F0.imprint","IMPRINT",EDGE,{"derivedFrom":sQuery(id+"F0.wireOp",EDGE,"d3a582e7-9daa-4fbb-a9f5-0dde8734c2e9.3.24.0")}),1.0]])]});
            var Q8;
            Q8=makeQuery(id+"F0.imprint","IMPRINT",FACE,{"disambiguationData":[TD([[makeQuery(id+"F0.imprint","IMPRINT",EDGE,{"derivedFrom":sQuery(id+"F0.wireOp",EDGE,"fde40906-ddec-4d3f-884f-99e619e92358.3.23.0")}),1.0]])]});
            var Q9;
            Q9=makeQuery(id+"F0.imprint","IMPRINT",FACE,{"disambiguationData":[TD([[makeQuery(id+"F0.imprint","IMPRINT",EDGE,{"derivedFrom":sQuery(id+"F0.wireOp",EDGE,"29f070b2-9a51-4b1b-9724-e17aadd86ff1.3.2.0")}),1.0]])]});
            var Q10;
            Q10=makeQuery(id+"F0.imprint","IMPRINT",FACE,{"disambiguationData":[TD([[makeQuery(id+"F0.imprint","IMPRINT",EDGE,{"derivedFrom":sQuery(id+"F0.wireOp",EDGE,"29f070b2-9a51-4b1b-9724-e17aadd86ff1.3.3.0")}),1.0]])]});
            var Q11;
            Q11=makeQuery(id+"F0.imprint","IMPRINT",FACE,{"disambiguationData":[TD([[makeQuery(id+"F0.imprint","IMPRINT",EDGE,{"derivedFrom":sQuery(id+"F0.wireOp",EDGE,"29f070b2-9a51-4b1b-9724-e17aadd86ff1.3.4.0")}),1.0]])]});
            var Q12;
            Q12=makeQuery(id+"F0.imprint","IMPRINT",FACE,{"disambiguationData":[TD([[makeQuery(id+"F0.imprint","IMPRINT",EDGE,{"derivedFrom":sQuery(id+"F0.wireOp",EDGE,"29f070b2-9a51-4b1b-9724-e17aadd86ff1.3.5.0")}),1.0]])]});
            var Q13;
            Q13=makeQuery(id+"F0.imprint","IMPRINT",FACE,{"disambiguationData":[TD([[makeQuery(id+"F0.imprint","IMPRINT",EDGE,{"derivedFrom":sQuery(id+"F0.wireOp",EDGE,"29f070b2-9a51-4b1b-9724-e17aadd86ff1.3.6.0")}),1.0]])]});
            var Q14;
            Q14=makeQuery(id+"F0.imprint","IMPRINT",FACE,{"disambiguationData":[TD([[makeQuery(id+"F0.imprint","IMPRINT",EDGE,{"derivedFrom":sQuery(id+"F0.wireOp",EDGE,"29f070b2-9a51-4b1b-9724-e17aadd86ff1.3.7.0")}),1.0]])]});
            var Q15;
            Q15=makeQuery(id+"F0.imprint","IMPRINT",FACE,{"disambiguationData":[TD([[makeQuery(id+"F0.imprint","IMPRINT",EDGE,{"derivedFrom":sQuery(id+"F0.wireOp",EDGE,"29f070b2-9a51-4b1b-9724-e17aadd86ff1.3.8.0")}),1.0]])]});
            var Q16;
            Q16=makeQuery(id+"F0.imprint","IMPRINT",FACE,{"disambiguationData":[TD([[makeQuery(id+"F0.imprint","IMPRINT",EDGE,{"derivedFrom":sQuery(id+"F0.wireOp",EDGE,"29f070b2-9a51-4b1b-9724-e17aadd86ff1.3.9.0")}),1.0]])]});
            var Q17;
            Q17=makeQuery(id+"F0.imprint","IMPRINT",FACE,{"disambiguationData":[TD([[makeQuery(id+"F0.imprint","IMPRINT",EDGE,{"derivedFrom":sQuery(id+"F0.wireOp",EDGE,"29f070b2-9a51-4b1b-9724-e17aadd86ff1.3.10.0")}),1.0]])]});
            var Q18;
            Q18=makeQuery(id+"F0.imprint","IMPRINT",FACE,{"disambiguationData":[TD([[makeQuery(id+"F0.imprint","IMPRINT",EDGE,{"derivedFrom":sQuery(id+"F0.wireOp",EDGE,"29f070b2-9a51-4b1b-9724-e17aadd86ff1.3.11.0")}),1.0]])]});
            var Q19;
            Q19=makeQuery(id+"F0.imprint","IMPRINT",FACE,{"disambiguationData":[TD([[makeQuery(id+"F0.imprint","IMPRINT",EDGE,{"derivedFrom":sQuery(id+"F0.wireOp",EDGE,"29f070b2-9a51-4b1b-9724-e17aadd86ff1.3.12.0")}),1.0]])]});
            var Q20;
            Q20=makeQuery(id+"F0.imprint","IMPRINT",FACE,{"disambiguationData":[TD([[makeQuery(id+"F0.imprint","IMPRINT",EDGE,{"derivedFrom":sQuery(id+"F0.wireOp",EDGE,"29f070b2-9a51-4b1b-9724-e17aadd86ff1.3.13.0")}),1.0]])]});
            var Q21;
            Q21=makeQuery(id+"F0.imprint","IMPRINT",FACE,{"disambiguationData":[TD([[makeQuery(id+"F0.imprint","IMPRINT",EDGE,{"derivedFrom":sQuery(id+"F0.wireOp",EDGE,"29f070b2-9a51-4b1b-9724-e17aadd86ff1.3.14.0")}),1.0]])]});
            var Q22;
            Q22=makeQuery(id+"F0.imprint","IMPRINT",FACE,{"disambiguationData":[TD([[makeQuery(id+"F0.imprint","IMPRINT",EDGE,{"derivedFrom":sQuery(id+"F0.wireOp",EDGE,"29f070b2-9a51-4b1b-9724-e17aadd86ff1.3.15.0")}),1.0]])]});
            var Q23;
            Q23=makeQuery(id+"F0.imprint","IMPRINT",FACE,{"disambiguationData":[TD([[makeQuery(id+"F0.imprint","IMPRINT",EDGE,{"derivedFrom":sQuery(id+"F0.wireOp",EDGE,"29f070b2-9a51-4b1b-9724-e17aadd86ff1.3.16.0")}),1.0]])]});
            var Q24;
            Q24=makeQuery(id+"F0.imprint","IMPRINT",FACE,{"disambiguationData":[TD([[makeQuery(id+"F0.imprint","IMPRINT",EDGE,{"derivedFrom":sQuery(id+"F0.wireOp",EDGE,"29f070b2-9a51-4b1b-9724-e17aadd86ff1.3.17.0")}),1.0]])]});
            var Q25;
            Q25=makeQuery(id+"F0.imprint","IMPRINT",FACE,{"disambiguationData":[TD([[makeQuery(id+"F0.imprint","IMPRINT",EDGE,{"derivedFrom":sQuery(id+"F0.wireOp",EDGE,"29f070b2-9a51-4b1b-9724-e17aadd86ff1.3.18.0")}),1.0]])]});
            var Q26;
            Q26=makeQuery(id+"F0.imprint","IMPRINT",FACE,{"disambiguationData":[TD([[makeQuery(id+"F0.imprint","IMPRINT",EDGE,{"derivedFrom":sQuery(id+"F0.wireOp",EDGE,"29f070b2-9a51-4b1b-9724-e17aadd86ff1.3.19.0")}),1.0]])]});
            var Q27;
            Q27=makeQuery(id+"F0.imprint","IMPRINT",FACE,{"disambiguationData":[TD([[makeQuery(id+"F0.imprint","IMPRINT",EDGE,{"derivedFrom":sQuery(id+"F0.wireOp",EDGE,"dbf09b4b-9e03-4a88-8ff8-c06494b98a75.3.20.0")}),1.0]])]});
            var Q28;
            Q28=makeQuery(id+"F0.imprint","IMPRINT",FACE,{"disambiguationData":[TD([[makeQuery(id+"F0.imprint","IMPRINT",EDGE,{"derivedFrom":sQuery(id+"F0.wireOp",EDGE,"dbf09b4b-9e03-4a88-8ff8-c06494b98a75.3.21.0")}),1.0]])]});
            var Q29;
            Q29=makeQuery(id+"F0.imprint","IMPRINT",FACE,{"disambiguationData":[TD([[makeQuery(id+"F0.imprint","IMPRINT",EDGE,{"derivedFrom":sQuery(id+"F0.wireOp",EDGE,"db47fc5c-4f4c-4138-ad39-1181877ca8ed.3.22.0")}),1.0]])]});
            var Q30;
            Q30=makeQuery(id+"F0.imprint","IMPRINT",FACE,{"disambiguationData":[TD([[makeQuery(id+"F0.imprint","IMPRINT",EDGE,{"derivedFrom":sQuery(id+"F0.wireOp",EDGE,"E8.3.29.0")}),1.0]])]});
            var Q31;
            Q31=makeQuery(id+"F0.imprint","IMPRINT",FACE,{"disambiguationData":[TD([[makeQuery(id+"F0.imprint","IMPRINT",EDGE,{"derivedFrom":sQuery(id+"F0.wireOp",EDGE,"E8.3.28.0")}),1.0]])]});
            var Q32;
            Q32=makeQuery(id+"F0.imprint","IMPRINT",FACE,{"disambiguationData":[TD([[makeQuery(id+"F0.imprint","IMPRINT",EDGE,{"derivedFrom":sQuery(id+"F0.wireOp",EDGE,"E8.3.27.0")}),1.0]])]});
            var Q33;
            Q33=makeQuery(id+"F0.imprint","IMPRINT",FACE,{"disambiguationData":[TD([[makeQuery(id+"F0.imprint","IMPRINT",EDGE,{"derivedFrom":sQuery(id+"F0.wireOp",EDGE,"E8.3.26.0")}),1.0]])]});
            var Q34;
            Q34=makeQuery(id+"F0.imprint","IMPRINT",FACE,{"disambiguationData":[TD([[makeQuery(id+"F0.imprint","IMPRINT",EDGE,{"derivedFrom":sQuery(id+"F0.wireOp",EDGE,"E8.3.25.0")}),1.0]])]});
            var Q35;
            Q35=makeQuery(id+"F0.imprint","IMPRINT",FACE,{"disambiguationData":[TD([[makeQuery(id+"F0.imprint","IMPRINT",EDGE,{"derivedFrom":sQuery(id+"F0.wireOp",EDGE,"E8.3.24.0")}),1.0]])]});
            var Q36;
            Q36=makeQuery(id+"F0.imprint","IMPRINT",FACE,{"disambiguationData":[TD([[makeQuery(id+"F0.imprint","IMPRINT",EDGE,{"derivedFrom":sQuery(id+"F0.wireOp",EDGE,"E8.3.23.0")}),1.0]])]});
            var Q37;
            Q37=makeQuery(id+"F0.imprint","IMPRINT",FACE,{"disambiguationData":[TD([[makeQuery(id+"F0.imprint","IMPRINT",EDGE,{"derivedFrom":sQuery(id+"F0.wireOp",EDGE,"E8.3.22.0")}),1.0]])]});
            var Q38;
            Q38=makeQuery(id+"F0.imprint","IMPRINT",FACE,{"disambiguationData":[TD([[makeQuery(id+"F0.imprint","IMPRINT",EDGE,{"derivedFrom":sQuery(id+"F0.wireOp",EDGE,"E8.3.21.0")}),1.0]])]});
            var Q39;
            Q39=makeQuery(id+"F0.imprint","IMPRINT",FACE,{"disambiguationData":[TD([[makeQuery(id+"F0.imprint","IMPRINT",EDGE,{"derivedFrom":sQuery(id+"F0.wireOp",EDGE,"E8.3.20.0")}),1.0]])]});
            var Q40;
            Q40=makeQuery(id+"F0.imprint","IMPRINT",FACE,{"disambiguationData":[TD([[makeQuery(id+"F0.imprint","IMPRINT",EDGE,{"derivedFrom":sQuery(id+"F0.wireOp",EDGE,"E8.3.19.0")}),1.0]])]});
            var Q41;
            Q41=makeQuery(id+"F0.imprint","IMPRINT",FACE,{"disambiguationData":[TD([[makeQuery(id+"F0.imprint","IMPRINT",EDGE,{"derivedFrom":sQuery(id+"F0.wireOp",EDGE,"E8.3.18.0")}),1.0]])]});
            var Q42;
            Q42=makeQuery(id+"F0.imprint","IMPRINT",FACE,{"disambiguationData":[TD([[makeQuery(id+"F0.imprint","IMPRINT",EDGE,{"derivedFrom":sQuery(id+"F0.wireOp",EDGE,"E8.3.17.0")}),1.0]])]});
            var Q43;
            Q43=makeQuery(id+"F0.imprint","IMPRINT",FACE,{"disambiguationData":[TD([[makeQuery(id+"F0.imprint","IMPRINT",EDGE,{"derivedFrom":sQuery(id+"F0.wireOp",EDGE,"E8.3.16.0")}),1.0]])]});
            var Q44;
            Q44=makeQuery(id+"F0.imprint","IMPRINT",FACE,{"disambiguationData":[TD([[makeQuery(id+"F0.imprint","IMPRINT",EDGE,{"derivedFrom":sQuery(id+"F0.wireOp",EDGE,"E8.3.15.0")}),1.0]])]});
            var Q45;
            Q45=makeQuery(id+"F0.imprint","IMPRINT",FACE,{"disambiguationData":[TD([[makeQuery(id+"F0.imprint","IMPRINT",EDGE,{"derivedFrom":sQuery(id+"F0.wireOp",EDGE,"E8.3.14.0")}),1.0]])]});
            var Q46;
            Q46=makeQuery(id+"F0.imprint","IMPRINT",FACE,{"disambiguationData":[TD([[makeQuery(id+"F0.imprint","IMPRINT",EDGE,{"derivedFrom":sQuery(id+"F0.wireOp",EDGE,"E8.3.13.0")}),1.0]])]});
            var Q47;
            Q47=makeQuery(id+"F0.imprint","IMPRINT",FACE,{"disambiguationData":[TD([[makeQuery(id+"F0.imprint","IMPRINT",EDGE,{"derivedFrom":sQuery(id+"F0.wireOp",EDGE,"E8.3.12.0")}),1.0]])]});
            var Q48;
            Q48=makeQuery(id+"F0.imprint","IMPRINT",FACE,{"disambiguationData":[TD([[makeQuery(id+"F0.imprint","IMPRINT",EDGE,{"derivedFrom":sQuery(id+"F0.wireOp",EDGE,"E8.3.11.0")}),1.0]])]});
            var Q49;
            Q49=makeQuery(id+"F0.imprint","IMPRINT",FACE,{"disambiguationData":[TD([[makeQuery(id+"F0.imprint","IMPRINT",EDGE,{"derivedFrom":sQuery(id+"F0.wireOp",EDGE,"E8.3.10.0")}),1.0]])]});
            var Q50;
            Q50=makeQuery(id+"F0.imprint","IMPRINT",FACE,{"disambiguationData":[TD([[makeQuery(id+"F0.imprint","IMPRINT",EDGE,{"derivedFrom":sQuery(id+"F0.wireOp",EDGE,"E8.3.9.0")}),1.0]])]});
            var Q51;
            Q51=makeQuery(id+"F0.imprint","IMPRINT",FACE,{"disambiguationData":[TD([[makeQuery(id+"F0.imprint","IMPRINT",EDGE,{"derivedFrom":sQuery(id+"F0.wireOp",EDGE,"E8.3.8.0")}),1.0]])]});
            var Q52;
            Q52=makeQuery(id+"F0.imprint","IMPRINT",FACE,{"disambiguationData":[TD([[makeQuery(id+"F0.imprint","IMPRINT",EDGE,{"derivedFrom":sQuery(id+"F0.wireOp",EDGE,"E8.3.7.0")}),1.0]])]});
            var Q53;
            Q53=makeQuery(id+"F0.imprint","IMPRINT",FACE,{"disambiguationData":[TD([[makeQuery(id+"F0.imprint","IMPRINT",EDGE,{"derivedFrom":sQuery(id+"F0.wireOp",EDGE,"E8.3.6.0")}),1.0]])]});
            var Q54;
            Q54=makeQuery(id+"F0.imprint","IMPRINT",FACE,{"disambiguationData":[TD([[makeQuery(id+"F0.imprint","IMPRINT",EDGE,{"derivedFrom":sQuery(id+"F0.wireOp",EDGE,"E8.3.5.0")}),1.0]])]});
            var Q55;
            Q55=makeQuery(id+"F0.imprint","IMPRINT",FACE,{"disambiguationData":[TD([[makeQuery(id+"F0.imprint","IMPRINT",EDGE,{"derivedFrom":sQuery(id+"F0.wireOp",EDGE,"E8.3.4.0")}),1.0]])]});
            var Q56;
            Q56=makeQuery(id+"F0.imprint","IMPRINT",FACE,{"disambiguationData":[TD([[makeQuery(id+"F0.imprint","IMPRINT",EDGE,{"derivedFrom":sQuery(id+"F0.wireOp",EDGE,"E8.3.3.0")}),1.0]])]});
            var Q57;
            Q57=makeQuery(id+"F0.imprint","IMPRINT",FACE,{"disambiguationData":[TD([[makeQuery(id+"F0.imprint","IMPRINT",EDGE,{"derivedFrom":sQuery(id+"F0.wireOp",EDGE,"E8.3.2.0")}),1.0]])]});
            extrude(context, id + "F1", {"entities" : qUnion([Q0, Q1, Q2, Q3, Q4, Q5, Q6, Q7, Q8, Q9, Q10, Q11, Q12, Q13, Q14, Q15, Q16, Q17, Q18, Q19, Q20, Q21, Q22, Q23, Q24, Q25, Q26, Q27, Q28, Q29, Q30, Q31, Q32, Q33, Q34, Q35, Q36, Q37, Q38, Q39, Q40, Q41, Q42, Q43, Q44, Q45, Q46, Q47, Q48, Q49, Q50, Q51, Q52, Q53, Q54, Q55, Q56, Q57]), "depth" : 25.4 * mm});
        }
        {
            var Q0;
            Q0=makeQuery(id+"F1.opExtrude","CAP_FACE",FACE,{"disambiguationData":[OSD([sQuery(id+"F0.wireOp",EDGE,"E0"),sQuery(id+"F0.wireOp",EDGE,"E1"),sQuery(id+"F0.wireOp",EDGE,"E2"),sQuery(id+"F0.wireOp",EDGE,"E3.left"),sQuery(id+"F0.wireOp",EDGE,"E3.right"),sQuery(id+"F0.wireOp",EDGE,"E4"),sQuery(id+"F0.wireOp",EDGE,"E5.MirrorCS"),sQuery(id+"F0.wireOp",EDGE,"E6.trimOffspring"),sQuery(id+"F0.wireOp",EDGE,"E7.1.0"),sQuery(id+"F0.wireOp",EDGE,"E7.1.1"),sQuery(id+"F0.wireOp",EDGE,"E7.1.2"),sQuery(id+"F0.wireOp",EDGE,"E7.1.3"),sQuery(id+"F0.wireOp",EDGE,"E7.1.4"),sQuery(id+"F0.wireOp",EDGE,"E7.1.5"),sQuery(id+"F0.wireOp",EDGE,"E7.1.6"),sQuery(id+"F0.wireOp",EDGE,"E8.3.2.0"),sQuery(id+"F0.wireOp",EDGE,"E8.4.2.0"),sQuery(id+"F0.wireOp",EDGE,"E8.7.2.0"),sQuery(id+"F0.wireOp",EDGE,"E8.11.2.0"),sQuery(id+"F0.wireOp",EDGE,"E8.15.2.0"),sQuery(id+"F0.wireOp",EDGE,"E8.18.2.0"),sQuery(id+"F0.wireOp",EDGE,"E8.21.2.0"),sQuery(id+"F0.wireOp",EDGE,"E8.3.3.0"),sQuery(id+"F0.wireOp",EDGE,"E8.4.3.0"),sQuery(id+"F0.wireOp",EDGE,"E8.7.3.0"),sQuery(id+"F0.wireOp",EDGE,"E8.11.3.0"),sQuery(id+"F0.wireOp",EDGE,"E8.15.3.0"),sQuery(id+"F0.wireOp",EDGE,"E8.18.3.0"),sQuery(id+"F0.wireOp",EDGE,"E8.21.3.0"),sQuery(id+"F0.wireOp",EDGE,"E8.3.4.0"),sQuery(id+"F0.wireOp",EDGE,"E8.4.4.0"),sQuery(id+"F0.wireOp",EDGE,"E8.7.4.0"),sQuery(id+"F0.wireOp",EDGE,"E8.11.4.0"),sQuery(id+"F0.wireOp",EDGE,"E8.15.4.0"),sQuery(id+"F0.wireOp",EDGE,"E8.18.4.0"),sQuery(id+"F0.wireOp",EDGE,"E8.21.4.0"),sQuery(id+"F0.wireOp",EDGE,"E8.3.5.0"),sQuery(id+"F0.wireOp",EDGE,"E8.4.5.0"),sQuery(id+"F0.wireOp",EDGE,"E8.7.5.0"),sQuery(id+"F0.wireOp",EDGE,"E8.11.5.0"),sQuery(id+"F0.wireOp",EDGE,"E8.15.5.0"),sQuery(id+"F0.wireOp",EDGE,"E8.18.5.0"),sQuery(id+"F0.wireOp",EDGE,"E8.21.5.0"),sQuery(id+"F0.wireOp",EDGE,"E8.3.6.0"),sQuery(id+"F0.wireOp",EDGE,"E8.4.6.0"),sQuery(id+"F0.wireOp",EDGE,"E8.7.6.0"),sQuery(id+"F0.wireOp",EDGE,"E8.11.6.0"),sQuery(id+"F0.wireOp",EDGE,"E8.15.6.0"),sQuery(id+"F0.wireOp",EDGE,"E8.18.6.0"),sQuery(id+"F0.wireOp",EDGE,"E8.21.6.0"),sQuery(id+"F0.wireOp",EDGE,"E8.3.7.0"),sQuery(id+"F0.wireOp",EDGE,"E8.4.7.0"),sQuery(id+"F0.wireOp",EDGE,"E8.7.7.0"),sQuery(id+"F0.wireOp",EDGE,"E8.11.7.0"),sQuery(id+"F0.wireOp",EDGE,"E8.15.7.0"),sQuery(id+"F0.wireOp",EDGE,"E8.18.7.0"),sQuery(id+"F0.wireOp",EDGE,"E8.21.7.0"),sQuery(id+"F0.wireOp",EDGE,"E8.3.8.0"),sQuery(id+"F0.wireOp",EDGE,"E8.4.8.0"),sQuery(id+"F0.wireOp",EDGE,"E8.7.8.0"),sQuery(id+"F0.wireOp",EDGE,"E8.11.8.0"),sQuery(id+"F0.wireOp",EDGE,"E8.15.8.0"),sQuery(id+"F0.wireOp",EDGE,"E8.18.8.0"),sQuery(id+"F0.wireOp",EDGE,"E8.21.8.0"),sQuery(id+"F0.wireOp",EDGE,"E8.3.9.0"),sQuery(id+"F0.wireOp",EDGE,"E8.4.9.0"),sQuery(id+"F0.wireOp",EDGE,"E8.7.9.0"),sQuery(id+"F0.wireOp",EDGE,"E8.11.9.0"),sQuery(id+"F0.wireOp",EDGE,"E8.15.9.0"),sQuery(id+"F0.wireOp",EDGE,"E8.18.9.0"),sQuery(id+"F0.wireOp",EDGE,"E8.21.9.0"),sQuery(id+"F0.wireOp",EDGE,"E8.3.10.0"),sQuery(id+"F0.wireOp",EDGE,"E8.4.10.0"),sQuery(id+"F0.wireOp",EDGE,"E8.7.10.0"),sQuery(id+"F0.wireOp",EDGE,"E8.11.10.0"),sQuery(id+"F0.wireOp",EDGE,"E8.15.10.0"),sQuery(id+"F0.wireOp",EDGE,"E8.18.10.0"),sQuery(id+"F0.wireOp",EDGE,"E8.21.10.0"),sQuery(id+"F0.wireOp",EDGE,"E8.3.11.0"),sQuery(id+"F0.wireOp",EDGE,"E8.4.11.0"),sQuery(id+"F0.wireOp",EDGE,"E8.7.11.0"),sQuery(id+"F0.wireOp",EDGE,"E8.11.11.0"),sQuery(id+"F0.wireOp",EDGE,"E8.15.11.0"),sQuery(id+"F0.wireOp",EDGE,"E8.18.11.0"),sQuery(id+"F0.wireOp",EDGE,"E8.21.11.0"),sQuery(id+"F0.wireOp",EDGE,"E8.3.12.0"),sQuery(id+"F0.wireOp",EDGE,"E8.4.12.0"),sQuery(id+"F0.wireOp",EDGE,"E8.7.12.0"),sQuery(id+"F0.wireOp",EDGE,"E8.11.12.0"),sQuery(id+"F0.wireOp",EDGE,"E8.15.12.0"),sQuery(id+"F0.wireOp",EDGE,"E8.18.12.0"),sQuery(id+"F0.wireOp",EDGE,"E8.21.12.0"),sQuery(id+"F0.wireOp",EDGE,"E8.3.13.0"),sQuery(id+"F0.wireOp",EDGE,"E8.4.13.0"),sQuery(id+"F0.wireOp",EDGE,"E8.7.13.0"),sQuery(id+"F0.wireOp",EDGE,"E8.11.13.0"),sQuery(id+"F0.wireOp",EDGE,"E8.15.13.0"),sQuery(id+"F0.wireOp",EDGE,"E8.18.13.0"),sQuery(id+"F0.wireOp",EDGE,"E8.21.13.0"),sQuery(id+"F0.wireOp",EDGE,"E8.3.14.0"),sQuery(id+"F0.wireOp",EDGE,"E8.4.14.0"),sQuery(id+"F0.wireOp",EDGE,"E8.7.14.0"),sQuery(id+"F0.wireOp",EDGE,"E8.11.14.0"),sQuery(id+"F0.wireOp",EDGE,"E8.15.14.0"),sQuery(id+"F0.wireOp",EDGE,"E8.18.14.0"),sQuery(id+"F0.wireOp",EDGE,"E8.21.14.0"),sQuery(id+"F0.wireOp",EDGE,"E8.3.15.0"),sQuery(id+"F0.wireOp",EDGE,"E8.4.15.0"),sQuery(id+"F0.wireOp",EDGE,"E8.7.15.0"),sQuery(id+"F0.wireOp",EDGE,"E8.11.15.0"),sQuery(id+"F0.wireOp",EDGE,"E8.15.15.0"),sQuery(id+"F0.wireOp",EDGE,"E8.18.15.0"),sQuery(id+"F0.wireOp",EDGE,"E8.21.15.0"),sQuery(id+"F0.wireOp",EDGE,"E8.3.16.0"),sQuery(id+"F0.wireOp",EDGE,"E8.4.16.0"),sQuery(id+"F0.wireOp",EDGE,"E8.7.16.0"),sQuery(id+"F0.wireOp",EDGE,"E8.11.16.0"),sQuery(id+"F0.wireOp",EDGE,"E8.15.16.0"),sQuery(id+"F0.wireOp",EDGE,"E8.18.16.0"),sQuery(id+"F0.wireOp",EDGE,"E8.21.16.0"),sQuery(id+"F0.wireOp",EDGE,"E8.3.17.0"),sQuery(id+"F0.wireOp",EDGE,"E8.4.17.0"),sQuery(id+"F0.wireOp",EDGE,"E8.7.17.0"),sQuery(id+"F0.wireOp",EDGE,"E8.11.17.0"),sQuery(id+"F0.wireOp",EDGE,"E8.15.17.0"),sQuery(id+"F0.wireOp",EDGE,"E8.18.17.0"),sQuery(id+"F0.wireOp",EDGE,"E8.21.17.0"),sQuery(id+"F0.wireOp",EDGE,"E8.3.18.0"),sQuery(id+"F0.wireOp",EDGE,"E8.4.18.0"),sQuery(id+"F0.wireOp",EDGE,"E8.7.18.0"),sQuery(id+"F0.wireOp",EDGE,"E8.11.18.0"),sQuery(id+"F0.wireOp",EDGE,"E8.15.18.0"),sQuery(id+"F0.wireOp",EDGE,"E8.18.18.0"),sQuery(id+"F0.wireOp",EDGE,"E8.21.18.0"),sQuery(id+"F0.wireOp",EDGE,"E8.3.19.0"),sQuery(id+"F0.wireOp",EDGE,"E8.4.19.0"),sQuery(id+"F0.wireOp",EDGE,"E8.7.19.0"),sQuery(id+"F0.wireOp",EDGE,"E8.11.19.0"),sQuery(id+"F0.wireOp",EDGE,"E8.15.19.0"),sQuery(id+"F0.wireOp",EDGE,"E8.18.19.0"),sQuery(id+"F0.wireOp",EDGE,"E8.21.19.0"),sQuery(id+"F0.wireOp",EDGE,"E8.3.20.0"),sQuery(id+"F0.wireOp",EDGE,"E8.4.20.0"),sQuery(id+"F0.wireOp",EDGE,"E8.7.20.0"),sQuery(id+"F0.wireOp",EDGE,"E8.11.20.0"),sQuery(id+"F0.wireOp",EDGE,"E8.15.20.0"),sQuery(id+"F0.wireOp",EDGE,"E8.18.20.0"),sQuery(id+"F0.wireOp",EDGE,"E8.21.20.0"),sQuery(id+"F0.wireOp",EDGE,"E8.3.21.0"),sQuery(id+"F0.wireOp",EDGE,"E8.4.21.0"),sQuery(id+"F0.wireOp",EDGE,"E8.7.21.0"),sQuery(id+"F0.wireOp",EDGE,"E8.11.21.0"),sQuery(id+"F0.wireOp",EDGE,"E8.15.21.0"),sQuery(id+"F0.wireOp",EDGE,"E8.18.21.0"),sQuery(id+"F0.wireOp",EDGE,"E8.21.21.0"),sQuery(id+"F0.wireOp",EDGE,"E8.3.22.0"),sQuery(id+"F0.wireOp",EDGE,"E8.4.22.0"),sQuery(id+"F0.wireOp",EDGE,"E8.7.22.0"),sQuery(id+"F0.wireOp",EDGE,"E8.11.22.0"),sQuery(id+"F0.wireOp",EDGE,"E8.15.22.0"),sQuery(id+"F0.wireOp",EDGE,"E8.18.22.0"),sQuery(id+"F0.wireOp",EDGE,"E8.21.22.0"),sQuery(id+"F0.wireOp",EDGE,"E8.3.23.0"),sQuery(id+"F0.wireOp",EDGE,"E8.4.23.0"),sQuery(id+"F0.wireOp",EDGE,"E8.7.23.0"),sQuery(id+"F0.wireOp",EDGE,"E8.11.23.0"),sQuery(id+"F0.wireOp",EDGE,"E8.15.23.0"),sQuery(id+"F0.wireOp",EDGE,"E8.18.23.0"),sQuery(id+"F0.wireOp",EDGE,"E8.21.23.0"),sQuery(id+"F0.wireOp",EDGE,"E8.3.24.0"),sQuery(id+"F0.wireOp",EDGE,"E8.4.24.0"),sQuery(id+"F0.wireOp",EDGE,"E8.7.24.0"),sQuery(id+"F0.wireOp",EDGE,"E8.11.24.0"),sQuery(id+"F0.wireOp",EDGE,"E8.15.24.0"),sQuery(id+"F0.wireOp",EDGE,"E8.18.24.0"),sQuery(id+"F0.wireOp",EDGE,"E8.21.24.0"),sQuery(id+"F0.wireOp",EDGE,"E8.3.25.0"),sQuery(id+"F0.wireOp",EDGE,"E8.4.25.0"),sQuery(id+"F0.wireOp",EDGE,"E8.7.25.0"),sQuery(id+"F0.wireOp",EDGE,"E8.11.25.0"),sQuery(id+"F0.wireOp",EDGE,"E8.15.25.0"),sQuery(id+"F0.wireOp",EDGE,"E8.18.25.0"),sQuery(id+"F0.wireOp",EDGE,"E8.21.25.0"),sQuery(id+"F0.wireOp",EDGE,"E8.3.26.0"),sQuery(id+"F0.wireOp",EDGE,"E8.4.26.0"),sQuery(id+"F0.wireOp",EDGE,"E8.7.26.0"),sQuery(id+"F0.wireOp",EDGE,"E8.11.26.0"),sQuery(id+"F0.wireOp",EDGE,"E8.15.26.0"),sQuery(id+"F0.wireOp",EDGE,"E8.18.26.0"),sQuery(id+"F0.wireOp",EDGE,"E8.21.26.0"),sQuery(id+"F0.wireOp",EDGE,"E8.3.27.0"),sQuery(id+"F0.wireOp",EDGE,"E8.4.27.0"),sQuery(id+"F0.wireOp",EDGE,"E8.7.27.0"),sQuery(id+"F0.wireOp",EDGE,"E8.11.27.0"),sQuery(id+"F0.wireOp",EDGE,"E8.15.27.0"),sQuery(id+"F0.wireOp",EDGE,"E8.18.27.0"),sQuery(id+"F0.wireOp",EDGE,"E8.21.27.0"),sQuery(id+"F0.wireOp",EDGE,"E8.3.28.0"),sQuery(id+"F0.wireOp",EDGE,"E8.4.28.0"),sQuery(id+"F0.wireOp",EDGE,"E8.7.28.0"),sQuery(id+"F0.wireOp",EDGE,"E8.11.28.0"),sQuery(id+"F0.wireOp",EDGE,"E8.15.28.0"),sQuery(id+"F0.wireOp",EDGE,"E8.18.28.0"),sQuery(id+"F0.wireOp",EDGE,"E8.21.28.0"),sQuery(id+"F0.wireOp",EDGE,"E8.3.29.0"),sQuery(id+"F0.wireOp",EDGE,"E8.4.29.0"),sQuery(id+"F0.wireOp",EDGE,"E8.7.29.0"),sQuery(id+"F0.wireOp",EDGE,"E8.11.29.0"),sQuery(id+"F0.wireOp",EDGE,"E8.15.29.0"),sQuery(id+"F0.wireOp",EDGE,"E8.18.29.0"),sQuery(id+"F0.wireOp",EDGE,"E8.21.29.0")])],"isStart":false});
            var sketch = newSketch(context, id + "F2", { "sketchPlane" : qUnion([Q0])});
            skCircle(sketch, "E9", {"center": v(0, 0) * mm, "radius": 86.28 * mm});
            skSolve(sketch);
        }
        {
            var Q0;
            Q0 = qSketchRegion(id + "F2", true);
            extrude(context, id + "F3", {"entities" : qUnion([Q0]), "operationType" : NewBodyOperationType.ADD, "depth" : 6.35 * mm});
        }
        {
            var Q0;
            Q0=makeQuery(id+"F3.opExtrude","CAP_FACE",FACE,{"disambiguationData":[OSD([sQuery(id+"F2.wireOp",EDGE,"E9")])],"isStart":false});
            var sketch = newSketch(context, id + "F4", { "sketchPlane" : qUnion([Q0])});
            skArc(sketch, "E10", {"start": v(17.64, 188.67) * mm, "mid": v(0.2, 189.47) * mm, "end": v(-17.25, 188.67) * mm});
            skArc(sketch, "E11", {"start": v(-3.51, 94.15) * mm, "mid": v(0.2, -96.28) * mm, "end": v(3.9, 94.15) * mm});
            skArc(sketch, "E12", {"start": v(-3.51, 183.41) * mm, "mid": v(-9.77, 183.18) * mm, "end": v(-16, 182.74) * mm});
            skLineSegment(sketch, "E13.left", {"start": v(3.9, 183.41) * mm, "end": v(3.9, 94.15) * mm});
            skLineSegment(sketch, "E13.right", {"start": v(-3.51, 183.41) * mm, "end": v(-3.51, 94.15) * mm});
            skPoint(sketch, "E13.middle", {"position": v(0.2, 138.78) * mm});
            skLineSegment(sketch, "E14", {"start": v(-17.25, 188.67) * mm, "end": v(-16, 182.74) * mm});
            skLineSegment(sketch, "E15.MirrorCS", {"start": v(17.64, 188.67) * mm, "end": v(16.39, 182.74) * mm});
            skArc(sketch, "E16.trimOffspring", {"start": v(16.39, 182.74) * mm, "mid": v(10.15, 183.18) * mm, "end": v(3.9, 183.41) * mm});
            skArc(sketch, "E17.1.0", {"start": v(-22.19, 188.15) * mm, "mid": v(-39.42, 185.3) * mm, "end": v(-56.31, 180.9) * mm});
            skLineSegment(sketch, "E17.1.1", {"start": v(-56.31, 180.9) * mm, "end": v(-53.86, 175.35) * mm});
            skArc(sketch, "E17.1.2", {"start": v(-41.78, 178.61) * mm, "mid": v(-47.85, 177.08) * mm, "end": v(-53.86, 175.35) * mm});
            skArc(sketch, "E17.1.3", {"start": v(-22.17, 182.09) * mm, "mid": v(-28.37, 181.22) * mm, "end": v(-34.53, 180.15) * mm});
            skLineSegment(sketch, "E17.1.4", {"start": v(-22.19, 188.15) * mm, "end": v(-22.17, 182.09) * mm});
            skLineSegment(sketch, "E17.1.5", {"start": v(-34.53, 180.15) * mm, "end": v(-15.98, 92.84) * mm});
            skLineSegment(sketch, "E17.1.6", {"start": v(-41.78, 178.61) * mm, "end": v(-23.22, 91.3) * mm});
            skArc(sketch, "E18.3.2.0", {"start": v(-61.03, 179.37) * mm, "mid": v(-77.3, 173) * mm, "end": v(-92.9, 165.17) * mm});
            skLineSegment(sketch, "E18.4.2.0", {"start": v(-92.9, 165.17) * mm, "end": v(-89.35, 160.26) * mm});
            skArc(sketch, "E18.7.2.0", {"start": v(-78.21, 165.96) * mm, "mid": v(-83.83, 163.2) * mm, "end": v(-89.35, 160.26) * mm});
            skArc(sketch, "E18.11.2.0", {"start": v(-59.76, 173.44) * mm, "mid": v(-65.64, 171.3) * mm, "end": v(-71.45, 168.97) * mm});
            skLineSegment(sketch, "E18.15.2.0", {"start": v(-61.03, 179.37) * mm, "end": v(-59.76, 173.44) * mm});
            skLineSegment(sketch, "E18.18.2.0", {"start": v(-71.45, 168.97) * mm, "end": v(-35.14, 87.43) * mm});
            skLineSegment(sketch, "E18.21.2.0", {"start": v(-78.21, 165.96) * mm, "end": v(-41.9, 84.41) * mm});
            skArc(sketch, "E18.3.3.0", {"start": v(-97.2, 162.7) * mm, "mid": v(-111.78, 153.09) * mm, "end": v(-125.43, 142.19) * mm});
            skLineSegment(sketch, "E18.4.3.0", {"start": v(-125.43, 142.19) * mm, "end": v(-120.93, 138.12) * mm});
            skArc(sketch, "E18.7.3.0", {"start": v(-111.22, 146) * mm, "mid": v(-116.14, 142.15) * mm, "end": v(-120.93, 138.12) * mm});
            skArc(sketch, "E18.11.3.0", {"start": v(-94.72, 157.16) * mm, "mid": v(-100.03, 153.85) * mm, "end": v(-105.22, 150.36) * mm});
            skLineSegment(sketch, "E18.15.3.0", {"start": v(-97.2, 162.7) * mm, "end": v(-94.72, 157.16) * mm});
            skLineSegment(sketch, "E18.18.3.0", {"start": v(-105.22, 150.36) * mm, "end": v(-52.76, 78.15) * mm});
            skLineSegment(sketch, "E18.21.3.0", {"start": v(-111.22, 146) * mm, "end": v(-58.75, 73.8) * mm});
            skArc(sketch, "E18.3.4.0", {"start": v(-129.11, 138.87) * mm, "mid": v(-141.38, 126.44) * mm, "end": v(-152.46, 112.94) * mm});
            skLineSegment(sketch, "E18.4.4.0", {"start": v(-152.46, 112.94) * mm, "end": v(-147.21, 109.9) * mm});
            skArc(sketch, "E18.7.4.0", {"start": v(-139.35, 119.63) * mm, "mid": v(-143.37, 114.83) * mm, "end": v(-147.21, 109.9) * mm});
            skArc(sketch, "E18.11.4.0", {"start": v(-125.53, 133.97) * mm, "mid": v(-130.04, 129.63) * mm, "end": v(-134.4, 125.14) * mm});
            skLineSegment(sketch, "E18.15.4.0", {"start": v(-129.11, 138.87) * mm, "end": v(-125.53, 133.97) * mm});
            skLineSegment(sketch, "E18.18.4.0", {"start": v(-134.4, 125.14) * mm, "end": v(-68.06, 65.4) * mm});
            skLineSegment(sketch, "E18.21.4.0", {"start": v(-139.35, 119.63) * mm, "end": v(-73.02, 59.9) * mm});
            skArc(sketch, "E18.3.5.0", {"start": v(-155.37, 108.93) * mm, "mid": v(-164.79, 94.22) * mm, "end": v(-172.82, 78.71) * mm});
            skLineSegment(sketch, "E18.4.5.0", {"start": v(-172.82, 78.71) * mm, "end": v(-167.05, 76.82) * mm});
            skArc(sketch, "E18.7.5.0", {"start": v(-161.4, 87.98) * mm, "mid": v(-164.32, 82.45) * mm, "end": v(-167.05, 76.82) * mm});
            skArc(sketch, "E18.11.5.0", {"start": v(-150.86, 104.88) * mm, "mid": v(-154.36, 99.7) * mm, "end": v(-157.69, 94.4) * mm});
            skLineSegment(sketch, "E18.15.5.0", {"start": v(-155.37, 108.93) * mm, "end": v(-150.86, 104.88) * mm});
            skLineSegment(sketch, "E18.18.5.0", {"start": v(-157.69, 94.4) * mm, "end": v(-80.38, 49.77) * mm});
            skLineSegment(sketch, "E18.21.5.0", {"start": v(-161.4, 87.98) * mm, "end": v(-84.09, 43.35) * mm});
            skArc(sketch, "E18.3.6.0", {"start": v(-174.83, 74.18) * mm, "mid": v(-180.99, 57.84) * mm, "end": v(-185.62, 41) * mm});
            skLineSegment(sketch, "E18.4.6.0", {"start": v(-185.62, 41) * mm, "end": v(-179.59, 40.35) * mm});
            skArc(sketch, "E18.7.6.0", {"start": v(-176.37, 52.44) * mm, "mid": v(-178.08, 46.43) * mm, "end": v(-179.59, 40.35) * mm});
            skArc(sketch, "E18.11.6.0", {"start": v(-169.57, 71.16) * mm, "mid": v(-171.93, 65.36) * mm, "end": v(-174.08, 59.49) * mm});
            skLineSegment(sketch, "E18.15.6.0", {"start": v(-174.83, 74.18) * mm, "end": v(-169.57, 71.16) * mm});
            skLineSegment(sketch, "E18.18.6.0", {"start": v(-174.08, 59.49) * mm, "end": v(-89.18, 31.9) * mm});
            skLineSegment(sketch, "E18.21.6.0", {"start": v(-176.37, 52.44) * mm, "end": v(-91.47, 24.86) * mm});
            skArc(sketch, "E18.3.7.0", {"start": v(-186.65, 36.15) * mm, "mid": v(-189.27, 18.88) * mm, "end": v(-190.3, 1.45) * mm});
            skLineSegment(sketch, "E18.4.7.0", {"start": v(-190.3, 1.45) * mm, "end": v(-184.26, 2.07) * mm});
            skArc(sketch, "E18.7.7.0", {"start": v(-183.63, 14.57) * mm, "mid": v(-184.05, 8.32) * mm, "end": v(-184.26, 2.07) * mm});
            skArc(sketch, "E18.11.7.0", {"start": v(-180.87, 34.29) * mm, "mid": v(-181.97, 28.13) * mm, "end": v(-182.85, 21.93) * mm});
            skLineSegment(sketch, "E18.15.7.0", {"start": v(-186.65, 36.15) * mm, "end": v(-180.87, 34.29) * mm});
            skLineSegment(sketch, "E18.18.7.0", {"start": v(-182.85, 21.93) * mm, "end": v(-94.08, 12.6) * mm});
            skLineSegment(sketch, "E18.21.7.0", {"start": v(-183.63, 14.57) * mm, "end": v(-94.85, 5.24) * mm});
            skArc(sketch, "E18.3.8.0", {"start": v(-190.3, -3.5) * mm, "mid": v(-189.27, -20.94) * mm, "end": v(-186.65, -38.2) * mm});
            skLineSegment(sketch, "E18.4.8.0", {"start": v(-186.65, -38.2) * mm, "end": v(-180.87, -36.35) * mm});
            skArc(sketch, "E18.7.8.0", {"start": v(-182.85, -24) * mm, "mid": v(-181.97, -30.19) * mm, "end": v(-180.87, -36.35) * mm});
            skArc(sketch, "E18.11.8.0", {"start": v(-184.26, -4.13) * mm, "mid": v(-184.05, -10.38) * mm, "end": v(-183.63, -16.63) * mm});
            skLineSegment(sketch, "E18.15.8.0", {"start": v(-190.3, -3.5) * mm, "end": v(-184.26, -4.13) * mm});
            skLineSegment(sketch, "E18.18.8.0", {"start": v(-183.63, -16.63) * mm, "end": v(-94.85, -7.3) * mm});
            skLineSegment(sketch, "E18.21.8.0", {"start": v(-182.85, -24) * mm, "end": v(-94.08, -14.66) * mm});
            skArc(sketch, "E18.3.9.0", {"start": v(-185.62, -43.06) * mm, "mid": v(-180.99, -59.9) * mm, "end": v(-174.83, -76.24) * mm});
            skLineSegment(sketch, "E18.4.9.0", {"start": v(-174.83, -76.24) * mm, "end": v(-169.57, -73.22) * mm});
            skArc(sketch, "E18.7.9.0", {"start": v(-174.08, -61.55) * mm, "mid": v(-171.93, -67.42) * mm, "end": v(-169.57, -73.22) * mm});
            skArc(sketch, "E18.11.9.0", {"start": v(-179.59, -42.4) * mm, "mid": v(-178.08, -48.48) * mm, "end": v(-176.37, -54.5) * mm});
            skLineSegment(sketch, "E18.15.9.0", {"start": v(-185.62, -43.06) * mm, "end": v(-179.59, -42.4) * mm});
            skLineSegment(sketch, "E18.18.9.0", {"start": v(-176.37, -54.5) * mm, "end": v(-91.47, -26.92) * mm});
            skLineSegment(sketch, "E18.21.9.0", {"start": v(-174.08, -61.55) * mm, "end": v(-89.18, -33.96) * mm});
            skArc(sketch, "E18.3.10.0", {"start": v(-172.82, -80.77) * mm, "mid": v(-164.79, -96.28) * mm, "end": v(-155.37, -110.99) * mm});
            skLineSegment(sketch, "E18.4.10.0", {"start": v(-155.37, -110.99) * mm, "end": v(-150.86, -106.94) * mm});
            skArc(sketch, "E18.7.10.0", {"start": v(-157.69, -96.46) * mm, "mid": v(-154.36, -101.76) * mm, "end": v(-150.86, -106.94) * mm});
            skArc(sketch, "E18.11.10.0", {"start": v(-167.05, -78.88) * mm, "mid": v(-164.32, -84.51) * mm, "end": v(-161.4, -90.04) * mm});
            skLineSegment(sketch, "E18.15.10.0", {"start": v(-172.82, -80.77) * mm, "end": v(-167.05, -78.88) * mm});
            skLineSegment(sketch, "E18.18.10.0", {"start": v(-161.4, -90.04) * mm, "end": v(-84.09, -45.41) * mm});
            skLineSegment(sketch, "E18.21.10.0", {"start": v(-157.69, -96.46) * mm, "end": v(-80.38, -51.83) * mm});
            skArc(sketch, "E18.3.11.0", {"start": v(-152.46, -115) * mm, "mid": v(-141.38, -128.5) * mm, "end": v(-129.11, -140.93) * mm});
            skLineSegment(sketch, "E18.4.11.0", {"start": v(-129.11, -140.93) * mm, "end": v(-125.53, -136.03) * mm});
            skArc(sketch, "E18.7.11.0", {"start": v(-134.4, -127.2) * mm, "mid": v(-130.04, -131.69) * mm, "end": v(-125.53, -136.03) * mm});
            skArc(sketch, "E18.11.11.0", {"start": v(-147.21, -111.95) * mm, "mid": v(-143.37, -116.89) * mm, "end": v(-139.35, -121.7) * mm});
            skLineSegment(sketch, "E18.15.11.0", {"start": v(-152.46, -115) * mm, "end": v(-147.21, -111.95) * mm});
            skLineSegment(sketch, "E18.18.11.0", {"start": v(-139.35, -121.7) * mm, "end": v(-73.02, -61.96) * mm});
            skLineSegment(sketch, "E18.21.11.0", {"start": v(-134.4, -127.2) * mm, "end": v(-68.06, -67.47) * mm});
            skArc(sketch, "E18.3.12.0", {"start": v(-125.43, -144.25) * mm, "mid": v(-111.78, -155.15) * mm, "end": v(-97.2, -164.75) * mm});
            skLineSegment(sketch, "E18.4.12.0", {"start": v(-97.2, -164.75) * mm, "end": v(-94.72, -159.22) * mm});
            skArc(sketch, "E18.7.12.0", {"start": v(-105.22, -152.42) * mm, "mid": v(-100.03, -155.9) * mm, "end": v(-94.72, -159.22) * mm});
            skArc(sketch, "E18.11.12.0", {"start": v(-120.93, -140.18) * mm, "mid": v(-116.14, -144.2) * mm, "end": v(-111.22, -148.07) * mm});
            skLineSegment(sketch, "E18.15.12.0", {"start": v(-125.43, -144.25) * mm, "end": v(-120.93, -140.18) * mm});
            skLineSegment(sketch, "E18.18.12.0", {"start": v(-111.22, -148.07) * mm, "end": v(-58.75, -75.85) * mm});
            skLineSegment(sketch, "E18.21.12.0", {"start": v(-105.22, -152.42) * mm, "end": v(-52.76, -80.2) * mm});
            skArc(sketch, "E18.3.13.0", {"start": v(-92.9, -167.23) * mm, "mid": v(-77.3, -175.06) * mm, "end": v(-61.03, -181.42) * mm});
            skLineSegment(sketch, "E18.4.13.0", {"start": v(-61.03, -181.42) * mm, "end": v(-59.76, -175.5) * mm});
            skArc(sketch, "E18.7.13.0", {"start": v(-71.45, -171.03) * mm, "mid": v(-65.64, -173.36) * mm, "end": v(-59.76, -175.5) * mm});
            skArc(sketch, "E18.11.13.0", {"start": v(-89.35, -162.32) * mm, "mid": v(-83.83, -165.26) * mm, "end": v(-78.21, -168.02) * mm});
            skLineSegment(sketch, "E18.15.13.0", {"start": v(-92.9, -167.23) * mm, "end": v(-89.35, -162.32) * mm});
            skLineSegment(sketch, "E18.18.13.0", {"start": v(-78.21, -168.02) * mm, "end": v(-41.9, -86.47) * mm});
            skLineSegment(sketch, "E18.21.13.0", {"start": v(-71.45, -171.03) * mm, "end": v(-35.14, -89.48) * mm});
            skArc(sketch, "E18.3.14.0", {"start": v(-56.31, -182.96) * mm, "mid": v(-39.42, -187.37) * mm, "end": v(-22.19, -190.21) * mm});
            skLineSegment(sketch, "E18.4.14.0", {"start": v(-22.19, -190.21) * mm, "end": v(-22.17, -184.15) * mm});
            skArc(sketch, "E18.7.14.0", {"start": v(-34.53, -182.2) * mm, "mid": v(-28.37, -183.28) * mm, "end": v(-22.17, -184.15) * mm});
            skArc(sketch, "E18.11.14.0", {"start": v(-53.86, -177.41) * mm, "mid": v(-47.85, -179.14) * mm, "end": v(-41.78, -180.67) * mm});
            skLineSegment(sketch, "E18.15.14.0", {"start": v(-56.31, -182.96) * mm, "end": v(-53.86, -177.41) * mm});
            skLineSegment(sketch, "E18.18.14.0", {"start": v(-41.78, -180.67) * mm, "end": v(-23.22, -93.36) * mm});
            skLineSegment(sketch, "E18.21.14.0", {"start": v(-34.53, -182.2) * mm, "end": v(-15.98, -94.9) * mm});
            skArc(sketch, "E18.3.15.0", {"start": v(-17.25, -190.73) * mm, "mid": v(0.2, -191.53) * mm, "end": v(17.64, -190.73) * mm});
            skLineSegment(sketch, "E18.4.15.0", {"start": v(17.64, -190.73) * mm, "end": v(16.39, -184.8) * mm});
            skArc(sketch, "E18.7.15.0", {"start": v(3.9, -185.47) * mm, "mid": v(10.15, -185.24) * mm, "end": v(16.39, -184.8) * mm});
            skArc(sketch, "E18.11.15.0", {"start": v(-16, -184.8) * mm, "mid": v(-9.77, -185.24) * mm, "end": v(-3.51, -185.47) * mm});
            skLineSegment(sketch, "E18.15.15.0", {"start": v(-17.25, -190.73) * mm, "end": v(-16, -184.8) * mm});
            skLineSegment(sketch, "E18.18.15.0", {"start": v(-3.51, -185.47) * mm, "end": v(-3.51, -96.2) * mm});
            skLineSegment(sketch, "E18.21.15.0", {"start": v(3.9, -185.47) * mm, "end": v(3.9, -96.2) * mm});
            skArc(sketch, "E18.3.16.0", {"start": v(22.57, -190.21) * mm, "mid": v(39.8, -187.37) * mm, "end": v(56.7, -182.96) * mm});
            skLineSegment(sketch, "E18.4.16.0", {"start": v(56.7, -182.96) * mm, "end": v(54.24, -177.41) * mm});
            skArc(sketch, "E18.7.16.0", {"start": v(42.16, -180.67) * mm, "mid": v(48.23, -179.14) * mm, "end": v(54.24, -177.41) * mm});
            skArc(sketch, "E18.11.16.0", {"start": v(22.55, -184.15) * mm, "mid": v(28.75, -183.28) * mm, "end": v(34.92, -182.2) * mm});
            skLineSegment(sketch, "E18.15.16.0", {"start": v(22.57, -190.21) * mm, "end": v(22.55, -184.15) * mm});
            skLineSegment(sketch, "E18.18.16.0", {"start": v(34.92, -182.2) * mm, "end": v(16.36, -94.9) * mm});
            skLineSegment(sketch, "E18.21.16.0", {"start": v(42.16, -180.67) * mm, "end": v(23.6, -93.36) * mm});
            skArc(sketch, "E18.3.17.0", {"start": v(61.41, -181.42) * mm, "mid": v(77.67, -175.06) * mm, "end": v(93.29, -167.23) * mm});
            skLineSegment(sketch, "E18.4.17.0", {"start": v(93.29, -167.23) * mm, "end": v(89.73, -162.32) * mm});
            skArc(sketch, "E18.7.17.0", {"start": v(78.6, -168.02) * mm, "mid": v(84.21, -165.26) * mm, "end": v(89.73, -162.32) * mm});
            skArc(sketch, "E18.11.17.0", {"start": v(60.14, -175.5) * mm, "mid": v(66.02, -173.36) * mm, "end": v(71.83, -171.03) * mm});
            skLineSegment(sketch, "E18.15.17.0", {"start": v(61.41, -181.42) * mm, "end": v(60.14, -175.5) * mm});
            skLineSegment(sketch, "E18.18.17.0", {"start": v(71.83, -171.03) * mm, "end": v(35.52, -89.48) * mm});
            skLineSegment(sketch, "E18.21.17.0", {"start": v(78.6, -168.02) * mm, "end": v(42.29, -86.47) * mm});
            skArc(sketch, "E18.3.18.0", {"start": v(97.58, -164.75) * mm, "mid": v(112.16, -155.15) * mm, "end": v(125.8, -144.25) * mm});
            skLineSegment(sketch, "E18.4.18.0", {"start": v(125.8, -144.25) * mm, "end": v(121.31, -140.18) * mm});
            skArc(sketch, "E18.7.18.0", {"start": v(111.6, -148.07) * mm, "mid": v(116.52, -144.2) * mm, "end": v(121.31, -140.18) * mm});
            skArc(sketch, "E18.11.18.0", {"start": v(95.1, -159.22) * mm, "mid": v(100.41, -155.9) * mm, "end": v(105.6, -152.42) * mm});
            skLineSegment(sketch, "E18.15.18.0", {"start": v(97.58, -164.75) * mm, "end": v(95.1, -159.22) * mm});
            skLineSegment(sketch, "E18.18.18.0", {"start": v(105.6, -152.42) * mm, "end": v(53.14, -80.2) * mm});
            skLineSegment(sketch, "E18.21.18.0", {"start": v(111.6, -148.07) * mm, "end": v(59.13, -75.85) * mm});
            skArc(sketch, "E18.3.19.0", {"start": v(129.5, -140.93) * mm, "mid": v(141.76, -128.5) * mm, "end": v(152.84, -115) * mm});
            skLineSegment(sketch, "E18.4.19.0", {"start": v(152.84, -115) * mm, "end": v(147.6, -111.95) * mm});
            skArc(sketch, "E18.7.19.0", {"start": v(139.73, -121.7) * mm, "mid": v(143.75, -116.89) * mm, "end": v(147.6, -111.95) * mm});
            skArc(sketch, "E18.11.19.0", {"start": v(125.92, -136.03) * mm, "mid": v(130.42, -131.69) * mm, "end": v(134.78, -127.2) * mm});
            skLineSegment(sketch, "E18.15.19.0", {"start": v(129.5, -140.93) * mm, "end": v(125.92, -136.03) * mm});
            skLineSegment(sketch, "E18.18.19.0", {"start": v(134.78, -127.2) * mm, "end": v(68.44, -67.47) * mm});
            skLineSegment(sketch, "E18.21.19.0", {"start": v(139.73, -121.7) * mm, "end": v(73.4, -61.96) * mm});
            skArc(sketch, "E18.3.20.0", {"start": v(155.75, -110.99) * mm, "mid": v(165.17, -96.28) * mm, "end": v(173.2, -80.77) * mm});
            skLineSegment(sketch, "E18.4.20.0", {"start": v(173.2, -80.77) * mm, "end": v(167.44, -78.88) * mm});
            skArc(sketch, "E18.7.20.0", {"start": v(161.77, -90.04) * mm, "mid": v(164.7, -84.51) * mm, "end": v(167.44, -78.88) * mm});
            skArc(sketch, "E18.11.20.0", {"start": v(151.24, -106.94) * mm, "mid": v(154.74, -101.76) * mm, "end": v(158.07, -96.46) * mm});
            skLineSegment(sketch, "E18.15.20.0", {"start": v(155.75, -110.99) * mm, "end": v(151.24, -106.94) * mm});
            skLineSegment(sketch, "E18.18.20.0", {"start": v(158.07, -96.46) * mm, "end": v(80.77, -51.83) * mm});
            skLineSegment(sketch, "E18.21.20.0", {"start": v(161.77, -90.04) * mm, "end": v(84.47, -45.41) * mm});
            skArc(sketch, "E18.3.21.0", {"start": v(175.21, -76.24) * mm, "mid": v(181.37, -59.9) * mm, "end": v(186, -43.06) * mm});
            skLineSegment(sketch, "E18.4.21.0", {"start": v(186, -43.06) * mm, "end": v(179.97, -42.4) * mm});
            skArc(sketch, "E18.7.21.0", {"start": v(176.75, -54.5) * mm, "mid": v(178.46, -48.48) * mm, "end": v(179.97, -42.4) * mm});
            skArc(sketch, "E18.11.21.0", {"start": v(169.96, -73.22) * mm, "mid": v(172.3, -67.42) * mm, "end": v(174.46, -61.55) * mm});
            skLineSegment(sketch, "E18.15.21.0", {"start": v(175.21, -76.24) * mm, "end": v(169.96, -73.22) * mm});
            skLineSegment(sketch, "E18.18.21.0", {"start": v(174.46, -61.55) * mm, "end": v(89.57, -33.96) * mm});
            skLineSegment(sketch, "E18.21.21.0", {"start": v(176.75, -54.5) * mm, "end": v(91.85, -26.92) * mm});
            skArc(sketch, "E18.3.22.0", {"start": v(187.03, -38.2) * mm, "mid": v(189.65, -20.94) * mm, "end": v(190.67, -3.5) * mm});
            skLineSegment(sketch, "E18.4.22.0", {"start": v(190.67, -3.5) * mm, "end": v(184.64, -4.13) * mm});
            skArc(sketch, "E18.7.22.0", {"start": v(184, -16.63) * mm, "mid": v(184.43, -10.38) * mm, "end": v(184.64, -4.13) * mm});
            skArc(sketch, "E18.11.22.0", {"start": v(181.26, -36.35) * mm, "mid": v(182.35, -30.19) * mm, "end": v(183.23, -24) * mm});
            skLineSegment(sketch, "E18.15.22.0", {"start": v(187.03, -38.2) * mm, "end": v(181.26, -36.35) * mm});
            skLineSegment(sketch, "E18.18.22.0", {"start": v(183.23, -24) * mm, "end": v(94.46, -14.66) * mm});
            skLineSegment(sketch, "E18.21.22.0", {"start": v(184, -16.63) * mm, "end": v(95.23, -7.3) * mm});
            skArc(sketch, "E18.3.23.0", {"start": v(190.67, 1.45) * mm, "mid": v(189.65, 18.88) * mm, "end": v(187.03, 36.15) * mm});
            skLineSegment(sketch, "E18.4.23.0", {"start": v(187.03, 36.15) * mm, "end": v(181.26, 34.29) * mm});
            skArc(sketch, "E18.7.23.0", {"start": v(183.23, 21.93) * mm, "mid": v(182.35, 28.13) * mm, "end": v(181.26, 34.29) * mm});
            skArc(sketch, "E18.11.23.0", {"start": v(184.64, 2.07) * mm, "mid": v(184.43, 8.32) * mm, "end": v(184, 14.57) * mm});
            skLineSegment(sketch, "E18.15.23.0", {"start": v(190.67, 1.45) * mm, "end": v(184.64, 2.07) * mm});
            skLineSegment(sketch, "E18.18.23.0", {"start": v(184, 14.57) * mm, "end": v(95.23, 5.24) * mm});
            skLineSegment(sketch, "E18.21.23.0", {"start": v(183.23, 21.93) * mm, "end": v(94.46, 12.6) * mm});
            skArc(sketch, "E18.3.24.0", {"start": v(186, 41) * mm, "mid": v(181.37, 57.84) * mm, "end": v(175.21, 74.18) * mm});
            skLineSegment(sketch, "E18.4.24.0", {"start": v(175.21, 74.18) * mm, "end": v(169.96, 71.16) * mm});
            skArc(sketch, "E18.7.24.0", {"start": v(174.46, 59.49) * mm, "mid": v(172.3, 65.36) * mm, "end": v(169.96, 71.16) * mm});
            skArc(sketch, "E18.11.24.0", {"start": v(179.97, 40.35) * mm, "mid": v(178.46, 46.43) * mm, "end": v(176.75, 52.44) * mm});
            skLineSegment(sketch, "E18.15.24.0", {"start": v(186, 41) * mm, "end": v(179.97, 40.35) * mm});
            skLineSegment(sketch, "E18.18.24.0", {"start": v(176.75, 52.44) * mm, "end": v(91.85, 24.86) * mm});
            skLineSegment(sketch, "E18.21.24.0", {"start": v(174.46, 59.49) * mm, "end": v(89.57, 31.9) * mm});
            skArc(sketch, "E18.3.25.0", {"start": v(173.2, 78.71) * mm, "mid": v(165.17, 94.22) * mm, "end": v(155.75, 108.93) * mm});
            skLineSegment(sketch, "E18.4.25.0", {"start": v(155.75, 108.93) * mm, "end": v(151.24, 104.88) * mm});
            skArc(sketch, "E18.7.25.0", {"start": v(158.07, 94.4) * mm, "mid": v(154.74, 99.7) * mm, "end": v(151.24, 104.88) * mm});
            skArc(sketch, "E18.11.25.0", {"start": v(167.44, 76.82) * mm, "mid": v(164.7, 82.45) * mm, "end": v(161.77, 87.98) * mm});
            skLineSegment(sketch, "E18.15.25.0", {"start": v(173.2, 78.71) * mm, "end": v(167.44, 76.82) * mm});
            skLineSegment(sketch, "E18.18.25.0", {"start": v(161.77, 87.98) * mm, "end": v(84.47, 43.35) * mm});
            skLineSegment(sketch, "E18.21.25.0", {"start": v(158.07, 94.4) * mm, "end": v(80.77, 49.77) * mm});
            skArc(sketch, "E18.3.26.0", {"start": v(152.84, 112.94) * mm, "mid": v(141.76, 126.44) * mm, "end": v(129.5, 138.87) * mm});
            skLineSegment(sketch, "E18.4.26.0", {"start": v(129.5, 138.87) * mm, "end": v(125.92, 133.97) * mm});
            skArc(sketch, "E18.7.26.0", {"start": v(134.78, 125.14) * mm, "mid": v(130.42, 129.63) * mm, "end": v(125.92, 133.97) * mm});
            skArc(sketch, "E18.11.26.0", {"start": v(147.6, 109.9) * mm, "mid": v(143.75, 114.83) * mm, "end": v(139.73, 119.63) * mm});
            skLineSegment(sketch, "E18.15.26.0", {"start": v(152.84, 112.94) * mm, "end": v(147.6, 109.9) * mm});
            skLineSegment(sketch, "E18.18.26.0", {"start": v(139.73, 119.63) * mm, "end": v(73.4, 59.9) * mm});
            skLineSegment(sketch, "E18.21.26.0", {"start": v(134.78, 125.14) * mm, "end": v(68.44, 65.4) * mm});
            skArc(sketch, "E18.3.27.0", {"start": v(125.8, 142.19) * mm, "mid": v(112.16, 153.09) * mm, "end": v(97.58, 162.7) * mm});
            skLineSegment(sketch, "E18.4.27.0", {"start": v(97.58, 162.7) * mm, "end": v(95.1, 157.16) * mm});
            skArc(sketch, "E18.7.27.0", {"start": v(105.6, 150.36) * mm, "mid": v(100.41, 153.85) * mm, "end": v(95.1, 157.16) * mm});
            skArc(sketch, "E18.11.27.0", {"start": v(121.31, 138.12) * mm, "mid": v(116.52, 142.15) * mm, "end": v(111.6, 146) * mm});
            skLineSegment(sketch, "E18.15.27.0", {"start": v(125.8, 142.19) * mm, "end": v(121.31, 138.12) * mm});
            skLineSegment(sketch, "E18.18.27.0", {"start": v(111.6, 146) * mm, "end": v(59.13, 73.8) * mm});
            skLineSegment(sketch, "E18.21.27.0", {"start": v(105.6, 150.36) * mm, "end": v(53.14, 78.15) * mm});
            skArc(sketch, "E18.3.28.0", {"start": v(93.29, 165.17) * mm, "mid": v(77.67, 173) * mm, "end": v(61.41, 179.37) * mm});
            skLineSegment(sketch, "E18.4.28.0", {"start": v(61.41, 179.37) * mm, "end": v(60.14, 173.44) * mm});
            skArc(sketch, "E18.7.28.0", {"start": v(71.83, 168.97) * mm, "mid": v(66.02, 171.3) * mm, "end": v(60.14, 173.44) * mm});
            skArc(sketch, "E18.11.28.0", {"start": v(89.73, 160.26) * mm, "mid": v(84.21, 163.2) * mm, "end": v(78.6, 165.96) * mm});
            skLineSegment(sketch, "E18.15.28.0", {"start": v(93.29, 165.17) * mm, "end": v(89.73, 160.26) * mm});
            skLineSegment(sketch, "E18.18.28.0", {"start": v(78.6, 165.96) * mm, "end": v(42.29, 84.41) * mm});
            skLineSegment(sketch, "E18.21.28.0", {"start": v(71.83, 168.97) * mm, "end": v(35.52, 87.43) * mm});
            skArc(sketch, "E18.3.29.0", {"start": v(56.7, 180.9) * mm, "mid": v(39.8, 185.3) * mm, "end": v(22.57, 188.15) * mm});
            skLineSegment(sketch, "E18.4.29.0", {"start": v(22.57, 188.15) * mm, "end": v(22.55, 182.09) * mm});
            skArc(sketch, "E18.7.29.0", {"start": v(34.92, 180.15) * mm, "mid": v(28.75, 181.22) * mm, "end": v(22.55, 182.09) * mm});
            skArc(sketch, "E18.11.29.0", {"start": v(54.24, 175.35) * mm, "mid": v(48.23, 177.08) * mm, "end": v(42.16, 178.61) * mm});
            skLineSegment(sketch, "E18.15.29.0", {"start": v(56.7, 180.9) * mm, "end": v(54.24, 175.35) * mm});
            skLineSegment(sketch, "E18.18.29.0", {"start": v(42.16, 178.61) * mm, "end": v(23.6, 91.3) * mm});
            skLineSegment(sketch, "E18.21.29.0", {"start": v(34.92, 180.15) * mm, "end": v(16.36, 92.84) * mm});
            skSolve(sketch);
        }
        {
            var Q0;
            Q0 = qSketchRegion(id + "F4", true);
            extrude(context, id + "F5", {"entities" : qUnion([Q0]), "operationType" : NewBodyOperationType.ADD, "depth" : 25.4 * mm});
        }
    });
